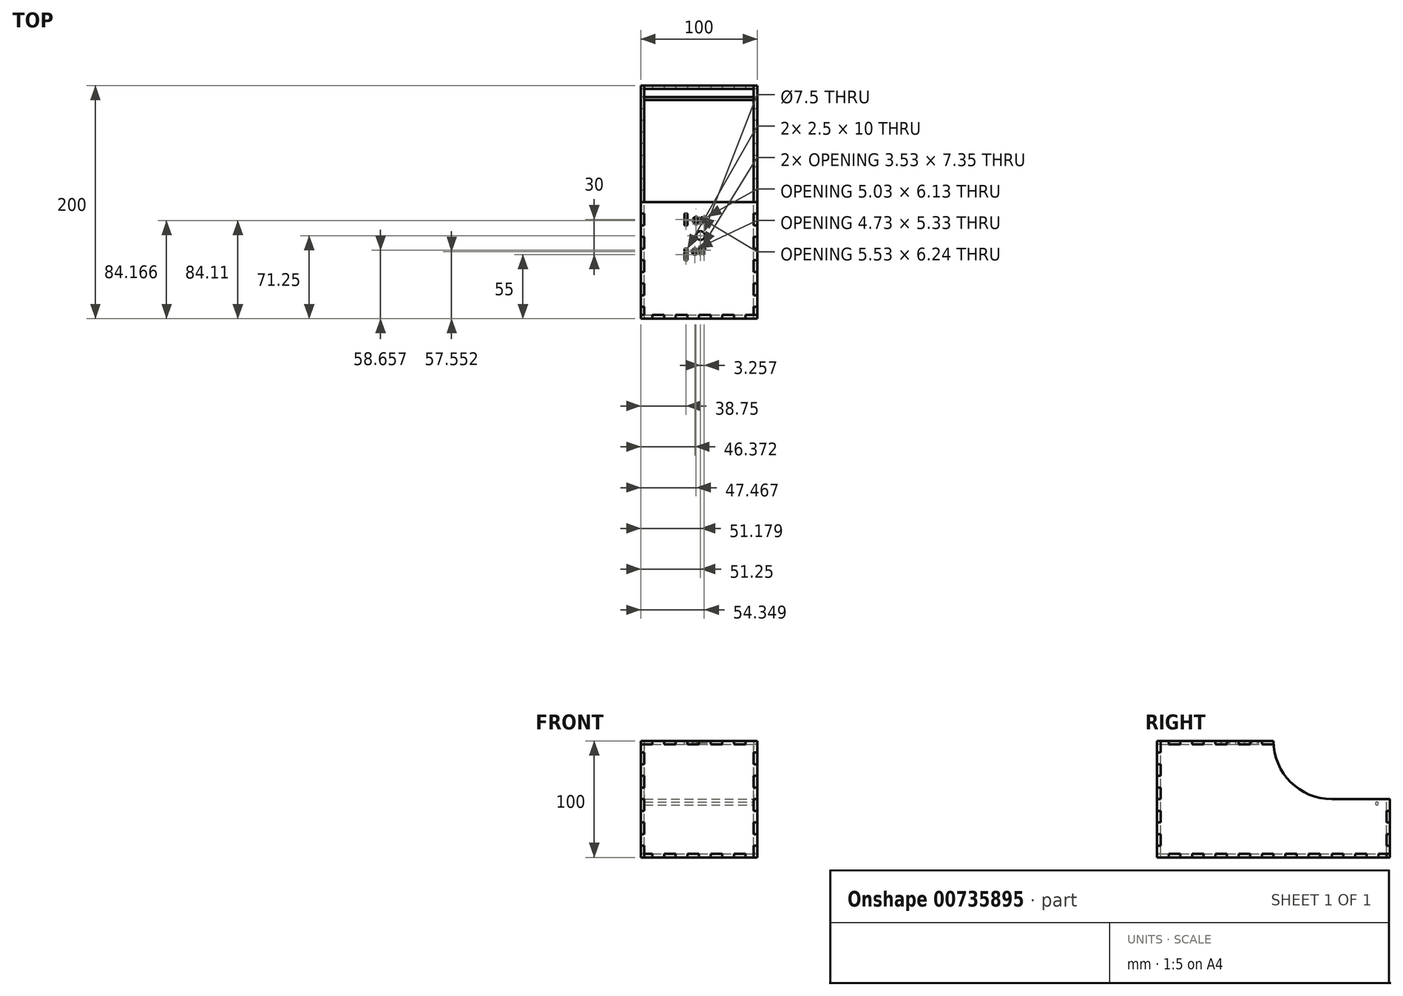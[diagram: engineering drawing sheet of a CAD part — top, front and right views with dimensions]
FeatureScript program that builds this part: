
annotation { "Feature Type Name" : "Feature", "Feature Type Description" : "" }
export const myFeature = defineFeature(function(context is Context, id is Id, definition is map)
    precondition{}
    {
        {
            var Q0;
            Q0=qCreatedBy(makeId("Right.planeOp"),FACE);
            var sketch = newSketch(context, id + "F0", { "sketchPlane" : qUnion([Q0])});
            skLineSegment(sketch, "E0.bottom", {"start": v(3, 0) * mm, "end": v(10, 0) * mm});
            skLineSegment(sketch, "E0.top", {"start": v(0, -100) * mm, "end": v(10, -100) * mm});
            skLineSegment(sketch, "E0.left", {"start": v(0, -10) * mm, "end": v(0, -20) * mm});
            skLineSegment(sketch, "E0.right", {"start": v(200, -10) * mm, "end": v(200, -20) * mm});
            skArc(sketch, "E1", {"start": v(100, 0) * mm, "mid": v(114.64, -35.36) * mm, "end": v(150, -50) * mm});
            skLineSegment(sketch, "E2", {"start": v(200, -50) * mm, "end": v(150, -50) * mm});
            skLineSegment(sketch, "E3.bottom", {"start": v(0, -90) * mm, "end": v(3, -90) * mm});
            skLineSegment(sketch, "E3.top", {"start": v(0, -80) * mm, "end": v(3, -80) * mm});
            skLineSegment(sketch, "E3.right", {"start": v(3, -90) * mm, "end": v(3, -80) * mm});
            skLineSegment(sketch, "E4.trimOffspring", {"start": v(0, -90) * mm, "end": v(0, -100) * mm});
            skLineSegment(sketch, "E5.0.1.0", {"start": v(0, -70) * mm, "end": v(3, -70) * mm});
            skLineSegment(sketch, "E5.0.1.1", {"start": v(3, -70) * mm, "end": v(3, -60) * mm});
            skLineSegment(sketch, "E5.0.1.2", {"start": v(0, -60) * mm, "end": v(3, -60) * mm});
            skLineSegment(sketch, "E5.0.2.0", {"start": v(0, -50) * mm, "end": v(3, -50) * mm});
            skLineSegment(sketch, "E5.0.2.1", {"start": v(3, -50) * mm, "end": v(3, -40) * mm});
            skLineSegment(sketch, "E5.0.2.2", {"start": v(0, -40) * mm, "end": v(3, -40) * mm});
            skLineSegment(sketch, "E5.0.3.0", {"start": v(0, -30) * mm, "end": v(3, -30) * mm});
            skLineSegment(sketch, "E5.0.3.1", {"start": v(3, -30) * mm, "end": v(3, -20) * mm});
            skLineSegment(sketch, "E5.0.3.2", {"start": v(0, -20) * mm, "end": v(3, -20) * mm});
            skLineSegment(sketch, "E5.0.4.0", {"start": v(0, -10) * mm, "end": v(3, -10) * mm});
            skLineSegment(sketch, "E5.0.4.1", {"start": v(3, -10) * mm, "end": v(3, 0) * mm});
            skLineSegment(sketch, "E5.direction1", {"start": v(0, -90) * mm, "end": v(25, -90) * mm, "construction": true});
            skLineSegment(sketch, "E5.direction2", {"start": v(0, -90) * mm, "end": v(0, -70) * mm, "construction": true});
            skLineSegment(sketch, "E6.trimOffspring", {"start": v(0, -30) * mm, "end": v(0, -40) * mm});
            skLineSegment(sketch, "E7.trimOffspring", {"start": v(0, -50) * mm, "end": v(0, -60) * mm});
            skLineSegment(sketch, "E8.trimOffspring", {"start": v(0, -70) * mm, "end": v(0, -80) * mm});
            skLineSegment(sketch, "E9.top", {"start": v(10, -97) * mm, "end": v(20, -97) * mm});
            skLineSegment(sketch, "E9.left", {"start": v(10, -100) * mm, "end": v(10, -97) * mm});
            skLineSegment(sketch, "E9.right", {"start": v(20, -100) * mm, "end": v(20, -97) * mm});
            skLineSegment(sketch, "E10.trimOffspring", {"start": v(20, -100) * mm, "end": v(30, -100) * mm});
            skLineSegment(sketch, "E11.1.0.0", {"start": v(30, -97) * mm, "end": v(40, -97) * mm});
            skLineSegment(sketch, "E11.1.0.1", {"start": v(40, -100) * mm, "end": v(40, -97) * mm});
            skLineSegment(sketch, "E11.1.0.3", {"start": v(30, -100) * mm, "end": v(30, -97) * mm});
            skLineSegment(sketch, "E11.2.0.0", {"start": v(50, -97) * mm, "end": v(60, -97) * mm});
            skLineSegment(sketch, "E11.2.0.1", {"start": v(60, -100) * mm, "end": v(60, -97) * mm});
            skLineSegment(sketch, "E11.2.0.2", {"start": v(40, -100) * mm, "end": v(50, -100) * mm});
            skLineSegment(sketch, "E11.2.0.3", {"start": v(50, -100) * mm, "end": v(50, -97) * mm});
            skLineSegment(sketch, "E11.3.0.0", {"start": v(70, -97) * mm, "end": v(80, -97) * mm});
            skLineSegment(sketch, "E11.3.0.1", {"start": v(80, -100) * mm, "end": v(80, -97) * mm});
            skLineSegment(sketch, "E11.3.0.2", {"start": v(60, -100) * mm, "end": v(70, -100) * mm});
            skLineSegment(sketch, "E11.3.0.3", {"start": v(70, -100) * mm, "end": v(70, -97) * mm});
            skLineSegment(sketch, "E11.4.0.0", {"start": v(90, -97) * mm, "end": v(100, -97) * mm});
            skLineSegment(sketch, "E11.4.0.1", {"start": v(100, -100) * mm, "end": v(100, -97) * mm});
            skLineSegment(sketch, "E11.4.0.2", {"start": v(80, -100) * mm, "end": v(90, -100) * mm});
            skLineSegment(sketch, "E11.4.0.3", {"start": v(90, -100) * mm, "end": v(90, -97) * mm});
            skLineSegment(sketch, "E11.5.0.0", {"start": v(110, -97) * mm, "end": v(120, -97) * mm});
            skLineSegment(sketch, "E11.5.0.1", {"start": v(120, -100) * mm, "end": v(120, -97) * mm});
            skLineSegment(sketch, "E11.5.0.2", {"start": v(100, -100) * mm, "end": v(110, -100) * mm});
            skLineSegment(sketch, "E11.5.0.3", {"start": v(110, -100) * mm, "end": v(110, -97) * mm});
            skLineSegment(sketch, "E11.6.0.0", {"start": v(130, -97) * mm, "end": v(140, -97) * mm});
            skLineSegment(sketch, "E11.6.0.1", {"start": v(140, -100) * mm, "end": v(140, -97) * mm});
            skLineSegment(sketch, "E11.6.0.2", {"start": v(120, -100) * mm, "end": v(130, -100) * mm});
            skLineSegment(sketch, "E11.6.0.3", {"start": v(130, -100) * mm, "end": v(130, -97) * mm});
            skLineSegment(sketch, "E11.7.0.0", {"start": v(150, -97) * mm, "end": v(160, -97) * mm});
            skLineSegment(sketch, "E11.7.0.1", {"start": v(160, -100) * mm, "end": v(160, -97) * mm});
            skLineSegment(sketch, "E11.7.0.2", {"start": v(140, -100) * mm, "end": v(150, -100) * mm});
            skLineSegment(sketch, "E11.7.0.3", {"start": v(150, -100) * mm, "end": v(150, -97) * mm});
            skLineSegment(sketch, "E11.8.0.0", {"start": v(170, -97) * mm, "end": v(180, -97) * mm});
            skLineSegment(sketch, "E11.8.0.1", {"start": v(180, -100) * mm, "end": v(180, -97) * mm});
            skLineSegment(sketch, "E11.8.0.2", {"start": v(160, -100) * mm, "end": v(170, -100) * mm});
            skLineSegment(sketch, "E11.8.0.3", {"start": v(170, -100) * mm, "end": v(170, -97) * mm});
            skLineSegment(sketch, "E11.9.0.0", {"start": v(190, -97) * mm, "end": v(200, -97) * mm});
            skLineSegment(sketch, "E11.9.0.2", {"start": v(180, -100) * mm, "end": v(190, -100) * mm});
            skLineSegment(sketch, "E11.9.0.3", {"start": v(190, -100) * mm, "end": v(190, -97) * mm});
            skLineSegment(sketch, "E11.direction1", {"start": v(0, -100) * mm, "end": v(20, -100) * mm, "construction": true});
            skLineSegment(sketch, "E12.top", {"start": v(197, -10) * mm, "end": v(200, -10) * mm});
            skLineSegment(sketch, "E12.left", {"start": v(197, -3) * mm, "end": v(197, -10) * mm});
            skLineSegment(sketch, "E13.0.1.1", {"start": v(197, -20) * mm, "end": v(197, -30) * mm});
            skLineSegment(sketch, "E13.0.1.2", {"start": v(197, -30) * mm, "end": v(200, -30) * mm});
            skLineSegment(sketch, "E13.0.1.3", {"start": v(197, -20) * mm, "end": v(200, -20) * mm});
            skLineSegment(sketch, "E13.0.2.1", {"start": v(197, -40) * mm, "end": v(197, -50) * mm});
            skLineSegment(sketch, "E13.0.2.2", {"start": v(197, -50) * mm, "end": v(200, -50) * mm});
            skLineSegment(sketch, "E13.0.2.3", {"start": v(197, -40) * mm, "end": v(200, -40) * mm});
            skLineSegment(sketch, "E13.0.3.1", {"start": v(197, -60) * mm, "end": v(197, -70) * mm});
            skLineSegment(sketch, "E13.0.3.2", {"start": v(197, -70) * mm, "end": v(200, -70) * mm});
            skLineSegment(sketch, "E13.0.3.3", {"start": v(197, -60) * mm, "end": v(200, -60) * mm});
            skLineSegment(sketch, "E13.0.4.1", {"start": v(197, -80) * mm, "end": v(197, -90) * mm});
            skLineSegment(sketch, "E13.0.4.2", {"start": v(197, -90) * mm, "end": v(200, -90) * mm});
            skLineSegment(sketch, "E13.0.4.3", {"start": v(197, -80) * mm, "end": v(200, -80) * mm});
            skLineSegment(sketch, "E13.direction1", {"start": v(197, -10) * mm, "end": v(222, -10) * mm, "construction": true});
            skLineSegment(sketch, "E13.direction2", {"start": v(197, -10) * mm, "end": v(197, -30) * mm, "construction": true});
            skLineSegment(sketch, "E14.trimOffspring", {"start": v(200, -90) * mm, "end": v(200, -97) * mm});
            skLineSegment(sketch, "E15.trimOffspring", {"start": v(200, -70) * mm, "end": v(200, -80) * mm});
            skLineSegment(sketch, "E16.trimOffspring", {"start": v(200, -50) * mm, "end": v(200, -60) * mm});
            skLineSegment(sketch, "E17.trimOffspring", {"start": v(200, -30) * mm, "end": v(200, -40) * mm});
            skLineSegment(sketch, "E18.top", {"start": v(10, -3) * mm, "end": v(20, -3) * mm});
            skLineSegment(sketch, "E18.left", {"start": v(10, 0) * mm, "end": v(10, -3) * mm});
            skLineSegment(sketch, "E18.right", {"start": v(20, 0) * mm, "end": v(20, -3) * mm});
            skLineSegment(sketch, "E19.trimOffspring", {"start": v(20, 0) * mm, "end": v(30, 0) * mm});
            skLineSegment(sketch, "E20.1.0.0", {"start": v(30, -3) * mm, "end": v(40, -3) * mm});
            skLineSegment(sketch, "E20.1.0.1", {"start": v(40, 0) * mm, "end": v(40, -3) * mm});
            skLineSegment(sketch, "E20.1.0.2", {"start": v(30, 0) * mm, "end": v(30, -3) * mm});
            skLineSegment(sketch, "E20.2.0.0", {"start": v(50, -3) * mm, "end": v(60, -3) * mm});
            skLineSegment(sketch, "E20.2.0.1", {"start": v(60, 0) * mm, "end": v(60, -3) * mm});
            skLineSegment(sketch, "E20.2.0.2", {"start": v(50, 0) * mm, "end": v(50, -3) * mm});
            skLineSegment(sketch, "E20.3.0.0", {"start": v(70, -3) * mm, "end": v(80, -3) * mm});
            skLineSegment(sketch, "E20.3.0.1", {"start": v(80, 0) * mm, "end": v(80, -3) * mm});
            skLineSegment(sketch, "E20.3.0.2", {"start": v(70, 0) * mm, "end": v(70, -3) * mm});
            skLineSegment(sketch, "E20.4.0.0", {"start": v(90, -3) * mm, "end": v(100, -3) * mm});
            skLineSegment(sketch, "E20.4.0.1", {"start": v(100, 0) * mm, "end": v(100, -3) * mm});
            skLineSegment(sketch, "E20.4.0.2", {"start": v(90, 0) * mm, "end": v(90, -3) * mm});
            skLineSegment(sketch, "E20.5.0.0", {"start": v(110, -3) * mm, "end": v(120, -3) * mm});
            skLineSegment(sketch, "E20.5.0.1", {"start": v(120, 0) * mm, "end": v(120, -3) * mm});
            skLineSegment(sketch, "E20.5.0.2", {"start": v(110, 0) * mm, "end": v(110, -3) * mm});
            skLineSegment(sketch, "E20.6.0.0", {"start": v(130, -3) * mm, "end": v(140, -3) * mm});
            skLineSegment(sketch, "E20.6.0.1", {"start": v(140, 0) * mm, "end": v(140, -3) * mm});
            skLineSegment(sketch, "E20.6.0.2", {"start": v(130, 0) * mm, "end": v(130, -3) * mm});
            skLineSegment(sketch, "E20.7.0.0", {"start": v(150, -3) * mm, "end": v(160, -3) * mm});
            skLineSegment(sketch, "E20.7.0.1", {"start": v(160, 0) * mm, "end": v(160, -3) * mm});
            skLineSegment(sketch, "E20.7.0.2", {"start": v(150, 0) * mm, "end": v(150, -3) * mm});
            skLineSegment(sketch, "E20.8.0.0", {"start": v(170, -3) * mm, "end": v(180, -3) * mm});
            skLineSegment(sketch, "E20.8.0.1", {"start": v(180, 0) * mm, "end": v(180, -3) * mm});
            skLineSegment(sketch, "E20.8.0.2", {"start": v(170, 0) * mm, "end": v(170, -3) * mm});
            skLineSegment(sketch, "E20.9.0.0", {"start": v(190, -3) * mm, "end": v(200, -3) * mm});
            skLineSegment(sketch, "E20.9.0.2", {"start": v(190, 0) * mm, "end": v(190, -3) * mm});
            skLineSegment(sketch, "E20.direction1", {"start": v(10, -3) * mm, "end": v(30, -3) * mm, "construction": true});
            skLineSegment(sketch, "E21.trimOffspring", {"start": v(40, 0) * mm, "end": v(50, 0) * mm});
            skLineSegment(sketch, "E22.trimOffspring", {"start": v(60, 0) * mm, "end": v(70, 0) * mm});
            skLineSegment(sketch, "E23.trimOffspring", {"start": v(80, 0) * mm, "end": v(90, 0) * mm});
            skLineSegment(sketch, "E24.trimOffspring", {"start": v(100, 0) * mm, "end": v(110, 0) * mm});
            skLineSegment(sketch, "E25.trimOffspring", {"start": v(120, 0) * mm, "end": v(130, 0) * mm});
            skLineSegment(sketch, "E26.trimOffspring", {"start": v(140, 0) * mm, "end": v(150, 0) * mm});
            skLineSegment(sketch, "E27.trimOffspring", {"start": v(160, 0) * mm, "end": v(170, 0) * mm});
            skLineSegment(sketch, "E28.trimOffspring", {"start": v(180, 0) * mm, "end": v(190, 0) * mm});
            skSolve(sketch);
        }
        {
            var Q0;
            Q0=makeQuery(id+"F0.imprint","IMPRINT",FACE,{"disambiguationData":[TD([[makeQuery(id+"F0.imprint","IMPRINT",EDGE,{"derivedFrom":sQuery(id+"F0.wireOp",EDGE,"E0.bottom")}),-1.0]])]});
            extrude(context, id + "F1", {"entities" : qUnion([Q0]), "depth" : 3 * mm, "offsetDistance" : 25 * mm});
        }
        {
            var Q0;
            Q0=makeQuery(id+"F0.imprint","IMPRINT",FACE,{"disambiguationData":[TD([[makeQuery(id+"F0.imprint","IMPRINT",EDGE,{"derivedFrom":sQuery(id+"F0.wireOp",EDGE,"E0.right")}),-1.0]])]});
            extrude(context, id + "F2", {"entities" : qUnion([Q0]), "depth" : 3 * mm, "offsetDistance" : 25 * mm});
        }
        {
            var Q0;
            Q0=qCreatedBy(makeId("Front.planeOp"),FACE);
            var sketch = newSketch(context, id + "F3", { "sketchPlane" : qUnion([Q0])});
            skLineSegment(sketch, "E29.bottom", {"start": v(3, 0) * mm, "end": v(-7, 0) * mm});
            skLineSegment(sketch, "E29.top", {"start": v(3, -100) * mm, "end": v(-7, -100) * mm});
            skLineSegment(sketch, "E29.left", {"start": v(3, 0) * mm, "end": v(3, -100) * mm});
            skLineSegment(sketch, "E29.right", {"start": v(-97, -3) * mm, "end": v(-97, -100) * mm});
            skLineSegment(sketch, "E30.top", {"start": v(-97, -3) * mm, "end": v(-87, -3) * mm});
            skLineSegment(sketch, "E30.right", {"start": v(-87, 0) * mm, "end": v(-87, -3) * mm});
            skLineSegment(sketch, "E31.top", {"start": v(-97, -97) * mm, "end": v(-87, -97) * mm});
            skLineSegment(sketch, "E31.left", {"start": v(-97, -100) * mm, "end": v(-97, -97) * mm});
            skLineSegment(sketch, "E31.right", {"start": v(-87, -100) * mm, "end": v(-87, -97) * mm});
            skLineSegment(sketch, "E32.1.0.0", {"start": v(-67, 0) * mm, "end": v(-67, -3) * mm});
            skLineSegment(sketch, "E32.1.0.1", {"start": v(-77, 0) * mm, "end": v(-77, -3) * mm});
            skLineSegment(sketch, "E32.1.0.2", {"start": v(-77, -3) * mm, "end": v(-67, -3) * mm});
            skLineSegment(sketch, "E32.2.0.0", {"start": v(-47, 0) * mm, "end": v(-47, -3) * mm});
            skLineSegment(sketch, "E32.2.0.1", {"start": v(-57, 0) * mm, "end": v(-57, -3) * mm});
            skLineSegment(sketch, "E32.2.0.2", {"start": v(-57, -3) * mm, "end": v(-47, -3) * mm});
            skLineSegment(sketch, "E32.3.0.0", {"start": v(-27, 0) * mm, "end": v(-27, -3) * mm});
            skLineSegment(sketch, "E32.3.0.1", {"start": v(-37, 0) * mm, "end": v(-37, -3) * mm});
            skLineSegment(sketch, "E32.3.0.2", {"start": v(-37, -3) * mm, "end": v(-27, -3) * mm});
            skLineSegment(sketch, "E32.4.0.0", {"start": v(-7, 0) * mm, "end": v(-7, -3) * mm});
            skLineSegment(sketch, "E32.4.0.1", {"start": v(-17, 0) * mm, "end": v(-17, -3) * mm});
            skLineSegment(sketch, "E32.4.0.2", {"start": v(-17, -3) * mm, "end": v(-7, -3) * mm});
            skLineSegment(sketch, "E32.direction1", {"start": v(-97, -3) * mm, "end": v(-77, -3) * mm, "construction": true});
            skLineSegment(sketch, "E33.1.0.1", {"start": v(-77, -97) * mm, "end": v(-67, -97) * mm});
            skLineSegment(sketch, "E33.1.0.2", {"start": v(-77, -100) * mm, "end": v(-77, -97) * mm});
            skLineSegment(sketch, "E33.1.0.3", {"start": v(-67, -100) * mm, "end": v(-67, -97) * mm});
            skLineSegment(sketch, "E33.2.0.1", {"start": v(-57, -97) * mm, "end": v(-47, -97) * mm});
            skLineSegment(sketch, "E33.2.0.2", {"start": v(-57, -100) * mm, "end": v(-57, -97) * mm});
            skLineSegment(sketch, "E33.2.0.3", {"start": v(-47, -100) * mm, "end": v(-47, -97) * mm});
            skLineSegment(sketch, "E33.3.0.1", {"start": v(-37, -97) * mm, "end": v(-27, -97) * mm});
            skLineSegment(sketch, "E33.3.0.2", {"start": v(-37, -100) * mm, "end": v(-37, -97) * mm});
            skLineSegment(sketch, "E33.3.0.3", {"start": v(-27, -100) * mm, "end": v(-27, -97) * mm});
            skLineSegment(sketch, "E33.4.0.1", {"start": v(-17, -97) * mm, "end": v(-7, -97) * mm});
            skLineSegment(sketch, "E33.4.0.2", {"start": v(-17, -100) * mm, "end": v(-17, -97) * mm});
            skLineSegment(sketch, "E33.4.0.3", {"start": v(-7, -100) * mm, "end": v(-7, -97) * mm});
            skLineSegment(sketch, "E33.direction1", {"start": v(-87, -100) * mm, "end": v(-77, -100) * mm, "construction": true});
            skLineSegment(sketch, "E34.trimOffspring", {"start": v(-77, 0) * mm, "end": v(-87, 0) * mm});
            skLineSegment(sketch, "E35.trimOffspring", {"start": v(-57, 0) * mm, "end": v(-67, 0) * mm});
            skLineSegment(sketch, "E36.trimOffspring", {"start": v(-37, 0) * mm, "end": v(-47, 0) * mm});
            skLineSegment(sketch, "E37.trimOffspring", {"start": v(-17, 0) * mm, "end": v(-27, 0) * mm});
            skLineSegment(sketch, "E38.trimOffspring", {"start": v(-17, -100) * mm, "end": v(-27, -100) * mm});
            skLineSegment(sketch, "E39.trimOffspring", {"start": v(-37, -100) * mm, "end": v(-47, -100) * mm});
            skLineSegment(sketch, "E40.trimOffspring", {"start": v(-57, -100) * mm, "end": v(-67, -100) * mm});
            skLineSegment(sketch, "E41.trimOffspring", {"start": v(-77, -100) * mm, "end": v(-87, -100) * mm});
            skLineSegment(sketch, "E42", {"start": v(-97, -50) * mm, "end": v(3, -50) * mm});
            skSolve(sketch);
        }
        {
            var Q0;
            Q0=makeQuery(id+"F1.opExtrude","SWEPT_BODY",BODY,{"disambiguationData":[OSD([sQuery(id+"F0.wireOp",EDGE,"E0.bottom"),sQuery(id+"F0.wireOp",EDGE,"E0.top"),sQuery(id+"F0.wireOp",EDGE,"E0.left"),sQuery(id+"F0.wireOp",EDGE,"E1"),sQuery(id+"F0.wireOp",EDGE,"E2"),sQuery(id+"F0.wireOp",EDGE,"E3.bottom"),sQuery(id+"F0.wireOp",EDGE,"E3.top"),sQuery(id+"F0.wireOp",EDGE,"E3.right"),sQuery(id+"F0.wireOp",EDGE,"E4.trimOffspring"),sQuery(id+"F0.wireOp",EDGE,"E5.0.1.0"),sQuery(id+"F0.wireOp",EDGE,"E5.0.1.1"),sQuery(id+"F0.wireOp",EDGE,"E5.0.1.2"),sQuery(id+"F0.wireOp",EDGE,"E5.0.2.0"),sQuery(id+"F0.wireOp",EDGE,"E5.0.2.1"),sQuery(id+"F0.wireOp",EDGE,"E5.0.2.2"),sQuery(id+"F0.wireOp",EDGE,"E5.0.3.0"),sQuery(id+"F0.wireOp",EDGE,"E5.0.3.1"),sQuery(id+"F0.wireOp",EDGE,"E5.0.3.2"),sQuery(id+"F0.wireOp",EDGE,"E5.0.4.0"),sQuery(id+"F0.wireOp",EDGE,"E5.0.4.1"),sQuery(id+"F0.wireOp",EDGE,"E6.trimOffspring"),sQuery(id+"F0.wireOp",EDGE,"E7.trimOffspring"),sQuery(id+"F0.wireOp",EDGE,"E8.trimOffspring"),sQuery(id+"F0.wireOp",EDGE,"E9.top"),sQuery(id+"F0.wireOp",EDGE,"E9.left"),sQuery(id+"F0.wireOp",EDGE,"E9.right"),sQuery(id+"F0.wireOp",EDGE,"E11.1.0.0"),sQuery(id+"F0.wireOp",EDGE,"E11.1.0.1"),sQuery(id+"F0.wireOp",EDGE,"E10.trimOffspring"),sQuery(id+"F0.wireOp",EDGE,"E11.1.0.3"),sQuery(id+"F0.wireOp",EDGE,"E11.2.0.0"),sQuery(id+"F0.wireOp",EDGE,"E11.2.0.1"),sQuery(id+"F0.wireOp",EDGE,"E11.2.0.3"),sQuery(id+"F0.wireOp",EDGE,"E11.3.0.0"),sQuery(id+"F0.wireOp",EDGE,"E11.3.0.1"),sQuery(id+"F0.wireOp",EDGE,"E11.3.0.3"),sQuery(id+"F0.wireOp",EDGE,"E11.4.0.0"),sQuery(id+"F0.wireOp",EDGE,"E11.4.0.1"),sQuery(id+"F0.wireOp",EDGE,"E11.4.0.3"),sQuery(id+"F0.wireOp",EDGE,"E11.5.0.0"),sQuery(id+"F0.wireOp",EDGE,"E11.5.0.1"),sQuery(id+"F0.wireOp",EDGE,"E11.5.0.3"),sQuery(id+"F0.wireOp",EDGE,"E11.6.0.0"),sQuery(id+"F0.wireOp",EDGE,"E11.6.0.1"),sQuery(id+"F0.wireOp",EDGE,"E11.6.0.3"),sQuery(id+"F0.wireOp",EDGE,"E11.7.0.0"),sQuery(id+"F0.wireOp",EDGE,"E11.7.0.1"),sQuery(id+"F0.wireOp",EDGE,"E11.7.0.3"),sQuery(id+"F0.wireOp",EDGE,"E11.8.0.0"),sQuery(id+"F0.wireOp",EDGE,"E11.8.0.1"),sQuery(id+"F0.wireOp",EDGE,"E11.8.0.3"),sQuery(id+"F0.wireOp",EDGE,"E11.9.0.0"),sQuery(id+"F0.wireOp",EDGE,"E11.9.0.3"),sQuery(id+"F0.wireOp",EDGE,"E11.2.0.2"),sQuery(id+"F0.wireOp",EDGE,"E11.3.0.2"),sQuery(id+"F0.wireOp",EDGE,"E11.4.0.2"),sQuery(id+"F0.wireOp",EDGE,"E11.5.0.2"),sQuery(id+"F0.wireOp",EDGE,"E11.6.0.2"),sQuery(id+"F0.wireOp",EDGE,"E11.7.0.2"),sQuery(id+"F0.wireOp",EDGE,"E11.8.0.2"),sQuery(id+"F0.wireOp",EDGE,"E11.9.0.2"),sQuery(id+"F0.wireOp",EDGE,"E13.0.2.2"),sQuery(id+"F0.wireOp",EDGE,"E13.0.3.1"),sQuery(id+"F0.wireOp",EDGE,"E13.0.3.2"),sQuery(id+"F0.wireOp",EDGE,"E13.0.3.3"),sQuery(id+"F0.wireOp",EDGE,"E13.0.4.1"),sQuery(id+"F0.wireOp",EDGE,"E13.0.4.2"),sQuery(id+"F0.wireOp",EDGE,"E13.0.4.3"),sQuery(id+"F0.wireOp",EDGE,"E14.trimOffspring"),sQuery(id+"F0.wireOp",EDGE,"E15.trimOffspring"),sQuery(id+"F0.wireOp",EDGE,"E16.trimOffspring"),sQuery(id+"F0.wireOp",EDGE,"E18.top"),sQuery(id+"F0.wireOp",EDGE,"E18.left"),sQuery(id+"F0.wireOp",EDGE,"E18.right"),sQuery(id+"F0.wireOp",EDGE,"E19.trimOffspring"),sQuery(id+"F0.wireOp",EDGE,"E20.1.0.0"),sQuery(id+"F0.wireOp",EDGE,"E20.1.0.1"),sQuery(id+"F0.wireOp",EDGE,"E20.1.0.2"),sQuery(id+"F0.wireOp",EDGE,"E20.2.0.0"),sQuery(id+"F0.wireOp",EDGE,"E20.2.0.1"),sQuery(id+"F0.wireOp",EDGE,"E20.2.0.2"),sQuery(id+"F0.wireOp",EDGE,"E20.3.0.0"),sQuery(id+"F0.wireOp",EDGE,"E20.3.0.1"),sQuery(id+"F0.wireOp",EDGE,"E20.3.0.2"),sQuery(id+"F0.wireOp",EDGE,"E20.4.0.0"),sQuery(id+"F0.wireOp",EDGE,"E20.4.0.1"),sQuery(id+"F0.wireOp",EDGE,"E20.4.0.2"),sQuery(id+"F0.wireOp",EDGE,"E21.trimOffspring"),sQuery(id+"F0.wireOp",EDGE,"E22.trimOffspring"),sQuery(id+"F0.wireOp",EDGE,"E23.trimOffspring")])]});
            transform(context, id + "F4", {"entities" : qUnion([Q0]), "transformType" : TransformType.TRANSLATION_3D, "dx" : -97 * mm, "dy" : 0 * mm, "dz" : 0 * mm, "makeCopy" : true});
        }
        {
            var Q0;
            Q0=makeQuery(id+"F2.opExtrude","SWEPT_BODY",BODY,{"disambiguationData":[OSD([sQuery(id+"F0.wireOp",EDGE,"E0.right"),sQuery(id+"F0.wireOp",EDGE,"E1"),sQuery(id+"F0.wireOp",EDGE,"E2"),sQuery(id+"F0.wireOp",EDGE,"E12.top"),sQuery(id+"F0.wireOp",EDGE,"E12.left"),sQuery(id+"F0.wireOp",EDGE,"E13.0.1.1"),sQuery(id+"F0.wireOp",EDGE,"E13.0.1.2"),sQuery(id+"F0.wireOp",EDGE,"E13.0.1.3"),sQuery(id+"F0.wireOp",EDGE,"E13.0.2.1"),sQuery(id+"F0.wireOp",EDGE,"E13.0.2.3"),sQuery(id+"F0.wireOp",EDGE,"E17.trimOffspring"),sQuery(id+"F0.wireOp",EDGE,"E20.5.0.0"),sQuery(id+"F0.wireOp",EDGE,"E20.5.0.1"),sQuery(id+"F0.wireOp",EDGE,"E20.5.0.2"),sQuery(id+"F0.wireOp",EDGE,"E20.6.0.0"),sQuery(id+"F0.wireOp",EDGE,"E20.6.0.1"),sQuery(id+"F0.wireOp",EDGE,"E20.6.0.2"),sQuery(id+"F0.wireOp",EDGE,"E20.7.0.0"),sQuery(id+"F0.wireOp",EDGE,"E20.7.0.1"),sQuery(id+"F0.wireOp",EDGE,"E20.7.0.2"),sQuery(id+"F0.wireOp",EDGE,"E20.8.0.0"),sQuery(id+"F0.wireOp",EDGE,"E20.8.0.1"),sQuery(id+"F0.wireOp",EDGE,"E20.8.0.2"),sQuery(id+"F0.wireOp",EDGE,"E20.9.0.0"),sQuery(id+"F0.wireOp",EDGE,"E20.9.0.2"),sQuery(id+"F0.wireOp",EDGE,"E24.trimOffspring"),sQuery(id+"F0.wireOp",EDGE,"E25.trimOffspring"),sQuery(id+"F0.wireOp",EDGE,"E26.trimOffspring"),sQuery(id+"F0.wireOp",EDGE,"E27.trimOffspring"),sQuery(id+"F0.wireOp",EDGE,"E28.trimOffspring")])]});
            transform(context, id + "F5", {"entities" : qUnion([Q0]), "transformType" : TransformType.TRANSLATION_3D, "dx" : -97 * mm, "dy" : 0 * mm, "dz" : 0 * mm, "makeCopy" : true});
        }
        {
            var Q0;
            Q0=qSketchRegion(id+"F3",true);
            extrude(context, id + "F6", {"entities" : qUnion([Q0]), "depth" : -3 * mm, "offsetDistance" : 25 * mm});
        }
        {
            var Q0;
            Q0=makeQuery(id+"F4.opPattern","COPY",BODY,{"derivedFrom":makeQuery(id+"F1.opExtrude","SWEPT_BODY",BODY,{"disambiguationData":[OSD([sQuery(id+"F0.wireOp",EDGE,"E0.bottom"),sQuery(id+"F0.wireOp",EDGE,"E0.top"),sQuery(id+"F0.wireOp",EDGE,"E0.left"),sQuery(id+"F0.wireOp",EDGE,"E1"),sQuery(id+"F0.wireOp",EDGE,"E2"),sQuery(id+"F0.wireOp",EDGE,"E3.bottom"),sQuery(id+"F0.wireOp",EDGE,"E3.top"),sQuery(id+"F0.wireOp",EDGE,"E3.right"),sQuery(id+"F0.wireOp",EDGE,"E4.trimOffspring"),sQuery(id+"F0.wireOp",EDGE,"E5.0.1.0"),sQuery(id+"F0.wireOp",EDGE,"E5.0.1.1"),sQuery(id+"F0.wireOp",EDGE,"E5.0.1.2"),sQuery(id+"F0.wireOp",EDGE,"E5.0.2.0"),sQuery(id+"F0.wireOp",EDGE,"E5.0.2.1"),sQuery(id+"F0.wireOp",EDGE,"E5.0.2.2"),sQuery(id+"F0.wireOp",EDGE,"E5.0.3.0"),sQuery(id+"F0.wireOp",EDGE,"E5.0.3.1"),sQuery(id+"F0.wireOp",EDGE,"E5.0.3.2"),sQuery(id+"F0.wireOp",EDGE,"E5.0.4.0"),sQuery(id+"F0.wireOp",EDGE,"E5.0.4.1"),sQuery(id+"F0.wireOp",EDGE,"E6.trimOffspring"),sQuery(id+"F0.wireOp",EDGE,"E7.trimOffspring"),sQuery(id+"F0.wireOp",EDGE,"E8.trimOffspring"),sQuery(id+"F0.wireOp",EDGE,"E9.top"),sQuery(id+"F0.wireOp",EDGE,"E9.left"),sQuery(id+"F0.wireOp",EDGE,"E9.right"),sQuery(id+"F0.wireOp",EDGE,"E11.1.0.0"),sQuery(id+"F0.wireOp",EDGE,"E11.1.0.1"),sQuery(id+"F0.wireOp",EDGE,"E10.trimOffspring"),sQuery(id+"F0.wireOp",EDGE,"E11.1.0.3"),sQuery(id+"F0.wireOp",EDGE,"E11.2.0.0"),sQuery(id+"F0.wireOp",EDGE,"E11.2.0.1"),sQuery(id+"F0.wireOp",EDGE,"E11.2.0.3"),sQuery(id+"F0.wireOp",EDGE,"E11.3.0.0"),sQuery(id+"F0.wireOp",EDGE,"E11.3.0.1"),sQuery(id+"F0.wireOp",EDGE,"E11.3.0.3"),sQuery(id+"F0.wireOp",EDGE,"E11.4.0.0"),sQuery(id+"F0.wireOp",EDGE,"E11.4.0.1"),sQuery(id+"F0.wireOp",EDGE,"E11.4.0.3"),sQuery(id+"F0.wireOp",EDGE,"E11.5.0.0"),sQuery(id+"F0.wireOp",EDGE,"E11.5.0.1"),sQuery(id+"F0.wireOp",EDGE,"E11.5.0.3"),sQuery(id+"F0.wireOp",EDGE,"E11.6.0.0"),sQuery(id+"F0.wireOp",EDGE,"E11.6.0.1"),sQuery(id+"F0.wireOp",EDGE,"E11.6.0.3"),sQuery(id+"F0.wireOp",EDGE,"E11.7.0.0"),sQuery(id+"F0.wireOp",EDGE,"E11.7.0.1"),sQuery(id+"F0.wireOp",EDGE,"E11.7.0.3"),sQuery(id+"F0.wireOp",EDGE,"E11.8.0.0"),sQuery(id+"F0.wireOp",EDGE,"E11.8.0.1"),sQuery(id+"F0.wireOp",EDGE,"E11.8.0.3"),sQuery(id+"F0.wireOp",EDGE,"E11.9.0.0"),sQuery(id+"F0.wireOp",EDGE,"E11.9.0.3"),sQuery(id+"F0.wireOp",EDGE,"E11.2.0.2"),sQuery(id+"F0.wireOp",EDGE,"E11.3.0.2"),sQuery(id+"F0.wireOp",EDGE,"E11.4.0.2"),sQuery(id+"F0.wireOp",EDGE,"E11.5.0.2"),sQuery(id+"F0.wireOp",EDGE,"E11.6.0.2"),sQuery(id+"F0.wireOp",EDGE,"E11.7.0.2"),sQuery(id+"F0.wireOp",EDGE,"E11.8.0.2"),sQuery(id+"F0.wireOp",EDGE,"E11.9.0.2"),sQuery(id+"F0.wireOp",EDGE,"E13.0.2.2"),sQuery(id+"F0.wireOp",EDGE,"E13.0.3.1"),sQuery(id+"F0.wireOp",EDGE,"E13.0.3.2"),sQuery(id+"F0.wireOp",EDGE,"E13.0.3.3"),sQuery(id+"F0.wireOp",EDGE,"E13.0.4.1"),sQuery(id+"F0.wireOp",EDGE,"E13.0.4.2"),sQuery(id+"F0.wireOp",EDGE,"E13.0.4.3"),sQuery(id+"F0.wireOp",EDGE,"E14.trimOffspring"),sQuery(id+"F0.wireOp",EDGE,"E15.trimOffspring"),sQuery(id+"F0.wireOp",EDGE,"E16.trimOffspring"),sQuery(id+"F0.wireOp",EDGE,"E18.top"),sQuery(id+"F0.wireOp",EDGE,"E18.left"),sQuery(id+"F0.wireOp",EDGE,"E18.right"),sQuery(id+"F0.wireOp",EDGE,"E19.trimOffspring"),sQuery(id+"F0.wireOp",EDGE,"E20.1.0.0"),sQuery(id+"F0.wireOp",EDGE,"E20.1.0.1"),sQuery(id+"F0.wireOp",EDGE,"E20.1.0.2"),sQuery(id+"F0.wireOp",EDGE,"E20.2.0.0"),sQuery(id+"F0.wireOp",EDGE,"E20.2.0.1"),sQuery(id+"F0.wireOp",EDGE,"E20.2.0.2"),sQuery(id+"F0.wireOp",EDGE,"E20.3.0.0"),sQuery(id+"F0.wireOp",EDGE,"E20.3.0.1"),sQuery(id+"F0.wireOp",EDGE,"E20.3.0.2"),sQuery(id+"F0.wireOp",EDGE,"E20.4.0.0"),sQuery(id+"F0.wireOp",EDGE,"E20.4.0.1"),sQuery(id+"F0.wireOp",EDGE,"E20.4.0.2"),sQuery(id+"F0.wireOp",EDGE,"E21.trimOffspring"),sQuery(id+"F0.wireOp",EDGE,"E22.trimOffspring"),sQuery(id+"F0.wireOp",EDGE,"E23.trimOffspring")])]}),"instanceName":"1"});
            var Q1;
            Q1=makeQuery(id+"F1.opExtrude","SWEPT_BODY",BODY,{"disambiguationData":[OSD([sQuery(id+"F0.wireOp",EDGE,"E0.bottom"),sQuery(id+"F0.wireOp",EDGE,"E0.top"),sQuery(id+"F0.wireOp",EDGE,"E0.left"),sQuery(id+"F0.wireOp",EDGE,"E1"),sQuery(id+"F0.wireOp",EDGE,"E2"),sQuery(id+"F0.wireOp",EDGE,"E3.bottom"),sQuery(id+"F0.wireOp",EDGE,"E3.top"),sQuery(id+"F0.wireOp",EDGE,"E3.right"),sQuery(id+"F0.wireOp",EDGE,"E4.trimOffspring"),sQuery(id+"F0.wireOp",EDGE,"E5.0.1.0"),sQuery(id+"F0.wireOp",EDGE,"E5.0.1.1"),sQuery(id+"F0.wireOp",EDGE,"E5.0.1.2"),sQuery(id+"F0.wireOp",EDGE,"E5.0.2.0"),sQuery(id+"F0.wireOp",EDGE,"E5.0.2.1"),sQuery(id+"F0.wireOp",EDGE,"E5.0.2.2"),sQuery(id+"F0.wireOp",EDGE,"E5.0.3.0"),sQuery(id+"F0.wireOp",EDGE,"E5.0.3.1"),sQuery(id+"F0.wireOp",EDGE,"E5.0.3.2"),sQuery(id+"F0.wireOp",EDGE,"E5.0.4.0"),sQuery(id+"F0.wireOp",EDGE,"E5.0.4.1"),sQuery(id+"F0.wireOp",EDGE,"E6.trimOffspring"),sQuery(id+"F0.wireOp",EDGE,"E7.trimOffspring"),sQuery(id+"F0.wireOp",EDGE,"E8.trimOffspring"),sQuery(id+"F0.wireOp",EDGE,"E9.top"),sQuery(id+"F0.wireOp",EDGE,"E9.left"),sQuery(id+"F0.wireOp",EDGE,"E9.right"),sQuery(id+"F0.wireOp",EDGE,"E11.1.0.0"),sQuery(id+"F0.wireOp",EDGE,"E11.1.0.1"),sQuery(id+"F0.wireOp",EDGE,"E10.trimOffspring"),sQuery(id+"F0.wireOp",EDGE,"E11.1.0.3"),sQuery(id+"F0.wireOp",EDGE,"E11.2.0.0"),sQuery(id+"F0.wireOp",EDGE,"E11.2.0.1"),sQuery(id+"F0.wireOp",EDGE,"E11.2.0.3"),sQuery(id+"F0.wireOp",EDGE,"E11.3.0.0"),sQuery(id+"F0.wireOp",EDGE,"E11.3.0.1"),sQuery(id+"F0.wireOp",EDGE,"E11.3.0.3"),sQuery(id+"F0.wireOp",EDGE,"E11.4.0.0"),sQuery(id+"F0.wireOp",EDGE,"E11.4.0.1"),sQuery(id+"F0.wireOp",EDGE,"E11.4.0.3"),sQuery(id+"F0.wireOp",EDGE,"E11.5.0.0"),sQuery(id+"F0.wireOp",EDGE,"E11.5.0.1"),sQuery(id+"F0.wireOp",EDGE,"E11.5.0.3"),sQuery(id+"F0.wireOp",EDGE,"E11.6.0.0"),sQuery(id+"F0.wireOp",EDGE,"E11.6.0.1"),sQuery(id+"F0.wireOp",EDGE,"E11.6.0.3"),sQuery(id+"F0.wireOp",EDGE,"E11.7.0.0"),sQuery(id+"F0.wireOp",EDGE,"E11.7.0.1"),sQuery(id+"F0.wireOp",EDGE,"E11.7.0.3"),sQuery(id+"F0.wireOp",EDGE,"E11.8.0.0"),sQuery(id+"F0.wireOp",EDGE,"E11.8.0.1"),sQuery(id+"F0.wireOp",EDGE,"E11.8.0.3"),sQuery(id+"F0.wireOp",EDGE,"E11.9.0.0"),sQuery(id+"F0.wireOp",EDGE,"E11.9.0.3"),sQuery(id+"F0.wireOp",EDGE,"E11.2.0.2"),sQuery(id+"F0.wireOp",EDGE,"E11.3.0.2"),sQuery(id+"F0.wireOp",EDGE,"E11.4.0.2"),sQuery(id+"F0.wireOp",EDGE,"E11.5.0.2"),sQuery(id+"F0.wireOp",EDGE,"E11.6.0.2"),sQuery(id+"F0.wireOp",EDGE,"E11.7.0.2"),sQuery(id+"F0.wireOp",EDGE,"E11.8.0.2"),sQuery(id+"F0.wireOp",EDGE,"E11.9.0.2"),sQuery(id+"F0.wireOp",EDGE,"E13.0.2.2"),sQuery(id+"F0.wireOp",EDGE,"E13.0.3.1"),sQuery(id+"F0.wireOp",EDGE,"E13.0.3.2"),sQuery(id+"F0.wireOp",EDGE,"E13.0.3.3"),sQuery(id+"F0.wireOp",EDGE,"E13.0.4.1"),sQuery(id+"F0.wireOp",EDGE,"E13.0.4.2"),sQuery(id+"F0.wireOp",EDGE,"E13.0.4.3"),sQuery(id+"F0.wireOp",EDGE,"E14.trimOffspring"),sQuery(id+"F0.wireOp",EDGE,"E15.trimOffspring"),sQuery(id+"F0.wireOp",EDGE,"E16.trimOffspring"),sQuery(id+"F0.wireOp",EDGE,"E18.top"),sQuery(id+"F0.wireOp",EDGE,"E18.left"),sQuery(id+"F0.wireOp",EDGE,"E18.right"),sQuery(id+"F0.wireOp",EDGE,"E19.trimOffspring"),sQuery(id+"F0.wireOp",EDGE,"E20.1.0.0"),sQuery(id+"F0.wireOp",EDGE,"E20.1.0.1"),sQuery(id+"F0.wireOp",EDGE,"E20.1.0.2"),sQuery(id+"F0.wireOp",EDGE,"E20.2.0.0"),sQuery(id+"F0.wireOp",EDGE,"E20.2.0.1"),sQuery(id+"F0.wireOp",EDGE,"E20.2.0.2"),sQuery(id+"F0.wireOp",EDGE,"E20.3.0.0"),sQuery(id+"F0.wireOp",EDGE,"E20.3.0.1"),sQuery(id+"F0.wireOp",EDGE,"E20.3.0.2"),sQuery(id+"F0.wireOp",EDGE,"E20.4.0.0"),sQuery(id+"F0.wireOp",EDGE,"E20.4.0.1"),sQuery(id+"F0.wireOp",EDGE,"E20.4.0.2"),sQuery(id+"F0.wireOp",EDGE,"E21.trimOffspring"),sQuery(id+"F0.wireOp",EDGE,"E22.trimOffspring"),sQuery(id+"F0.wireOp",EDGE,"E23.trimOffspring")])]});
            var Q2;
            Q2=makeQuery(id+"F6.opExtrude","SWEPT_BODY",BODY,{"disambiguationData":[OSD([sQuery(id+"F3.wireOp",EDGE,"E29.bottom"),sQuery(id+"F3.wireOp",EDGE,"E29.top"),sQuery(id+"F3.wireOp",EDGE,"E29.left"),sQuery(id+"F3.wireOp",EDGE,"E29.right"),sQuery(id+"F3.wireOp",EDGE,"E30.top"),sQuery(id+"F3.wireOp",EDGE,"E30.right"),sQuery(id+"F3.wireOp",EDGE,"E31.top"),sQuery(id+"F3.wireOp",EDGE,"E31.right"),sQuery(id+"F3.wireOp",EDGE,"E32.1.0.0"),sQuery(id+"F3.wireOp",EDGE,"E32.1.0.1"),sQuery(id+"F3.wireOp",EDGE,"E32.1.0.2"),sQuery(id+"F3.wireOp",EDGE,"E32.2.0.0"),sQuery(id+"F3.wireOp",EDGE,"E32.2.0.1"),sQuery(id+"F3.wireOp",EDGE,"E32.2.0.2"),sQuery(id+"F3.wireOp",EDGE,"E32.3.0.0"),sQuery(id+"F3.wireOp",EDGE,"E32.3.0.1"),sQuery(id+"F3.wireOp",EDGE,"E32.3.0.2"),sQuery(id+"F3.wireOp",EDGE,"E32.4.0.0"),sQuery(id+"F3.wireOp",EDGE,"E32.4.0.1"),sQuery(id+"F3.wireOp",EDGE,"E32.4.0.2"),sQuery(id+"F3.wireOp",EDGE,"E33.1.0.1"),sQuery(id+"F3.wireOp",EDGE,"E33.1.0.2"),sQuery(id+"F3.wireOp",EDGE,"E33.1.0.3"),sQuery(id+"F3.wireOp",EDGE,"E33.2.0.1"),sQuery(id+"F3.wireOp",EDGE,"E33.2.0.2"),sQuery(id+"F3.wireOp",EDGE,"E33.2.0.3"),sQuery(id+"F3.wireOp",EDGE,"E33.3.0.1"),sQuery(id+"F3.wireOp",EDGE,"E33.3.0.2"),sQuery(id+"F3.wireOp",EDGE,"E33.3.0.3"),sQuery(id+"F3.wireOp",EDGE,"E33.4.0.1"),sQuery(id+"F3.wireOp",EDGE,"E33.4.0.2"),sQuery(id+"F3.wireOp",EDGE,"E33.4.0.3"),sQuery(id+"F3.wireOp",EDGE,"E34.trimOffspring"),sQuery(id+"F3.wireOp",EDGE,"E35.trimOffspring"),sQuery(id+"F3.wireOp",EDGE,"E36.trimOffspring"),sQuery(id+"F3.wireOp",EDGE,"E37.trimOffspring"),sQuery(id+"F3.wireOp",EDGE,"E38.trimOffspring"),sQuery(id+"F3.wireOp",EDGE,"E39.trimOffspring"),sQuery(id+"F3.wireOp",EDGE,"E40.trimOffspring"),sQuery(id+"F3.wireOp",EDGE,"E41.trimOffspring")])]});
            booleanBodies(context, id + "F7", {"operationType" : BooleanOperationType.SUBTRACTION, "tools" : qUnion([Q0, Q1]), "targets" : qUnion([Q2]), "keepTools" : true});
        }
        {
            var Q0;
            {var subQ1=sQuery(id+"F3.wireOp",EDGE,"E29.top");Q0=makeQuery(id+"F3.imprint","IMPRINT",FACE,{"disambiguationData":[TD([[makeQuery(id+"F3.imprint","IMPRINT",EDGE,{"derivedFrom":subQ1}),-1.0]])]});}
            extrude(context, id + "F8", {"entities" : qUnion([Q0]), "oppositeDirection" : true, "depth" : 200 * mm, "offsetDistance" : 25 * mm, "hasSecondDirection" : true, "secondDirectionOppositeDirection" : true, "secondDirectionDepth" : 197 * mm});
        }
        {
            var Q0;
            {var subQ0=sQuery(id+"F3.wireOp",EDGE,"E29.bottom");Q0=makeQuery(id+"F3.imprint","IMPRINT",FACE,{"disambiguationData":[TD([[makeQuery(id+"F3.imprint","IMPRINT",EDGE,{"derivedFrom":subQ0}),1.0]])]});}
            extrude(context, id + "F9", {"entities" : qUnion([Q0]), "oppositeDirection" : true, "depth" : 200 * mm, "offsetDistance" : 25 * mm, "hasSecondDirection" : true, "secondDirectionOppositeDirection" : true, "secondDirectionDepth" : 197 * mm});
        }
        {
            var Q0;
            Q0=makeQuery(id+"F2.opExtrude","SWEPT_BODY",BODY,{"disambiguationData":[OSD([sQuery(id+"F0.wireOp",EDGE,"E0.right"),sQuery(id+"F0.wireOp",EDGE,"E1"),sQuery(id+"F0.wireOp",EDGE,"E2"),sQuery(id+"F0.wireOp",EDGE,"E12.top"),sQuery(id+"F0.wireOp",EDGE,"E12.left"),sQuery(id+"F0.wireOp",EDGE,"E13.0.1.1"),sQuery(id+"F0.wireOp",EDGE,"E13.0.1.2"),sQuery(id+"F0.wireOp",EDGE,"E13.0.1.3"),sQuery(id+"F0.wireOp",EDGE,"E13.0.2.1"),sQuery(id+"F0.wireOp",EDGE,"E13.0.2.3"),sQuery(id+"F0.wireOp",EDGE,"E17.trimOffspring"),sQuery(id+"F0.wireOp",EDGE,"E20.5.0.0"),sQuery(id+"F0.wireOp",EDGE,"E20.5.0.1"),sQuery(id+"F0.wireOp",EDGE,"E20.5.0.2"),sQuery(id+"F0.wireOp",EDGE,"E20.6.0.0"),sQuery(id+"F0.wireOp",EDGE,"E20.6.0.1"),sQuery(id+"F0.wireOp",EDGE,"E20.6.0.2"),sQuery(id+"F0.wireOp",EDGE,"E20.7.0.0"),sQuery(id+"F0.wireOp",EDGE,"E20.7.0.1"),sQuery(id+"F0.wireOp",EDGE,"E20.7.0.2"),sQuery(id+"F0.wireOp",EDGE,"E20.8.0.0"),sQuery(id+"F0.wireOp",EDGE,"E20.8.0.1"),sQuery(id+"F0.wireOp",EDGE,"E20.8.0.2"),sQuery(id+"F0.wireOp",EDGE,"E20.9.0.0"),sQuery(id+"F0.wireOp",EDGE,"E20.9.0.2"),sQuery(id+"F0.wireOp",EDGE,"E24.trimOffspring"),sQuery(id+"F0.wireOp",EDGE,"E25.trimOffspring"),sQuery(id+"F0.wireOp",EDGE,"E26.trimOffspring"),sQuery(id+"F0.wireOp",EDGE,"E27.trimOffspring"),sQuery(id+"F0.wireOp",EDGE,"E28.trimOffspring")])]});
            var Q1;
            Q1=makeQuery(id+"F5.opPattern","COPY",BODY,{"derivedFrom":makeQuery(id+"F2.opExtrude","SWEPT_BODY",BODY,{"disambiguationData":[OSD([sQuery(id+"F0.wireOp",EDGE,"E0.right"),sQuery(id+"F0.wireOp",EDGE,"E1"),sQuery(id+"F0.wireOp",EDGE,"E2"),sQuery(id+"F0.wireOp",EDGE,"E12.top"),sQuery(id+"F0.wireOp",EDGE,"E12.left"),sQuery(id+"F0.wireOp",EDGE,"E13.0.1.1"),sQuery(id+"F0.wireOp",EDGE,"E13.0.1.2"),sQuery(id+"F0.wireOp",EDGE,"E13.0.1.3"),sQuery(id+"F0.wireOp",EDGE,"E13.0.2.1"),sQuery(id+"F0.wireOp",EDGE,"E13.0.2.3"),sQuery(id+"F0.wireOp",EDGE,"E17.trimOffspring"),sQuery(id+"F0.wireOp",EDGE,"E20.5.0.0"),sQuery(id+"F0.wireOp",EDGE,"E20.5.0.1"),sQuery(id+"F0.wireOp",EDGE,"E20.5.0.2"),sQuery(id+"F0.wireOp",EDGE,"E20.6.0.0"),sQuery(id+"F0.wireOp",EDGE,"E20.6.0.1"),sQuery(id+"F0.wireOp",EDGE,"E20.6.0.2"),sQuery(id+"F0.wireOp",EDGE,"E20.7.0.0"),sQuery(id+"F0.wireOp",EDGE,"E20.7.0.1"),sQuery(id+"F0.wireOp",EDGE,"E20.7.0.2"),sQuery(id+"F0.wireOp",EDGE,"E20.8.0.0"),sQuery(id+"F0.wireOp",EDGE,"E20.8.0.1"),sQuery(id+"F0.wireOp",EDGE,"E20.8.0.2"),sQuery(id+"F0.wireOp",EDGE,"E20.9.0.0"),sQuery(id+"F0.wireOp",EDGE,"E20.9.0.2"),sQuery(id+"F0.wireOp",EDGE,"E24.trimOffspring"),sQuery(id+"F0.wireOp",EDGE,"E25.trimOffspring"),sQuery(id+"F0.wireOp",EDGE,"E26.trimOffspring"),sQuery(id+"F0.wireOp",EDGE,"E27.trimOffspring"),sQuery(id+"F0.wireOp",EDGE,"E28.trimOffspring")])]}),"instanceName":"1"});
            var Q2;
            Q2=makeQuery(id+"F9.opExtrude","SWEPT_BODY",BODY,{"disambiguationData":[OSD([sQuery(id+"F3.wireOp",EDGE,"E29.bottom"),sQuery(id+"F3.wireOp",EDGE,"E29.left"),sQuery(id+"F3.wireOp",EDGE,"E29.right"),sQuery(id+"F3.wireOp",EDGE,"E30.top"),sQuery(id+"F3.wireOp",EDGE,"E30.right"),sQuery(id+"F3.wireOp",EDGE,"E32.1.0.0"),sQuery(id+"F3.wireOp",EDGE,"E32.1.0.1"),sQuery(id+"F3.wireOp",EDGE,"E32.1.0.2"),sQuery(id+"F3.wireOp",EDGE,"E32.2.0.0"),sQuery(id+"F3.wireOp",EDGE,"E32.2.0.1"),sQuery(id+"F3.wireOp",EDGE,"E32.2.0.2"),sQuery(id+"F3.wireOp",EDGE,"E32.3.0.0"),sQuery(id+"F3.wireOp",EDGE,"E32.3.0.1"),sQuery(id+"F3.wireOp",EDGE,"E32.3.0.2"),sQuery(id+"F3.wireOp",EDGE,"E32.4.0.0"),sQuery(id+"F3.wireOp",EDGE,"E32.4.0.1"),sQuery(id+"F3.wireOp",EDGE,"E32.4.0.2"),sQuery(id+"F3.wireOp",EDGE,"E34.trimOffspring"),sQuery(id+"F3.wireOp",EDGE,"E35.trimOffspring"),sQuery(id+"F3.wireOp",EDGE,"E36.trimOffspring"),sQuery(id+"F3.wireOp",EDGE,"E37.trimOffspring"),sQuery(id+"F3.wireOp",EDGE,"E42")])]});
            booleanBodies(context, id + "F10", {"operationType" : BooleanOperationType.SUBTRACTION, "tools" : qUnion([Q0, Q1]), "targets" : qUnion([Q2]), "keepTools" : true});
        }
        {
            var Q0;
            Q0=makeQuery(id+"F1.opExtrude","SWEPT_BODY",BODY,{"disambiguationData":[OSD([sQuery(id+"F0.wireOp",EDGE,"E0.bottom"),sQuery(id+"F0.wireOp",EDGE,"E0.top"),sQuery(id+"F0.wireOp",EDGE,"E0.left"),sQuery(id+"F0.wireOp",EDGE,"E1"),sQuery(id+"F0.wireOp",EDGE,"E2"),sQuery(id+"F0.wireOp",EDGE,"E3.bottom"),sQuery(id+"F0.wireOp",EDGE,"E3.top"),sQuery(id+"F0.wireOp",EDGE,"E3.right"),sQuery(id+"F0.wireOp",EDGE,"E4.trimOffspring"),sQuery(id+"F0.wireOp",EDGE,"E5.0.1.0"),sQuery(id+"F0.wireOp",EDGE,"E5.0.1.1"),sQuery(id+"F0.wireOp",EDGE,"E5.0.1.2"),sQuery(id+"F0.wireOp",EDGE,"E5.0.2.0"),sQuery(id+"F0.wireOp",EDGE,"E5.0.2.1"),sQuery(id+"F0.wireOp",EDGE,"E5.0.2.2"),sQuery(id+"F0.wireOp",EDGE,"E5.0.3.0"),sQuery(id+"F0.wireOp",EDGE,"E5.0.3.1"),sQuery(id+"F0.wireOp",EDGE,"E5.0.3.2"),sQuery(id+"F0.wireOp",EDGE,"E5.0.4.0"),sQuery(id+"F0.wireOp",EDGE,"E5.0.4.1"),sQuery(id+"F0.wireOp",EDGE,"E6.trimOffspring"),sQuery(id+"F0.wireOp",EDGE,"E7.trimOffspring"),sQuery(id+"F0.wireOp",EDGE,"E8.trimOffspring"),sQuery(id+"F0.wireOp",EDGE,"E9.top"),sQuery(id+"F0.wireOp",EDGE,"E9.left"),sQuery(id+"F0.wireOp",EDGE,"E9.right"),sQuery(id+"F0.wireOp",EDGE,"E11.1.0.0"),sQuery(id+"F0.wireOp",EDGE,"E11.1.0.1"),sQuery(id+"F0.wireOp",EDGE,"E10.trimOffspring"),sQuery(id+"F0.wireOp",EDGE,"E11.1.0.3"),sQuery(id+"F0.wireOp",EDGE,"E11.2.0.0"),sQuery(id+"F0.wireOp",EDGE,"E11.2.0.1"),sQuery(id+"F0.wireOp",EDGE,"E11.2.0.3"),sQuery(id+"F0.wireOp",EDGE,"E11.3.0.0"),sQuery(id+"F0.wireOp",EDGE,"E11.3.0.1"),sQuery(id+"F0.wireOp",EDGE,"E11.3.0.3"),sQuery(id+"F0.wireOp",EDGE,"E11.4.0.0"),sQuery(id+"F0.wireOp",EDGE,"E11.4.0.1"),sQuery(id+"F0.wireOp",EDGE,"E11.4.0.3"),sQuery(id+"F0.wireOp",EDGE,"E11.5.0.0"),sQuery(id+"F0.wireOp",EDGE,"E11.5.0.1"),sQuery(id+"F0.wireOp",EDGE,"E11.5.0.3"),sQuery(id+"F0.wireOp",EDGE,"E11.6.0.0"),sQuery(id+"F0.wireOp",EDGE,"E11.6.0.1"),sQuery(id+"F0.wireOp",EDGE,"E11.6.0.3"),sQuery(id+"F0.wireOp",EDGE,"E11.7.0.0"),sQuery(id+"F0.wireOp",EDGE,"E11.7.0.1"),sQuery(id+"F0.wireOp",EDGE,"E11.7.0.3"),sQuery(id+"F0.wireOp",EDGE,"E11.8.0.0"),sQuery(id+"F0.wireOp",EDGE,"E11.8.0.1"),sQuery(id+"F0.wireOp",EDGE,"E11.8.0.3"),sQuery(id+"F0.wireOp",EDGE,"E11.9.0.0"),sQuery(id+"F0.wireOp",EDGE,"E11.9.0.3"),sQuery(id+"F0.wireOp",EDGE,"E11.2.0.2"),sQuery(id+"F0.wireOp",EDGE,"E11.3.0.2"),sQuery(id+"F0.wireOp",EDGE,"E11.4.0.2"),sQuery(id+"F0.wireOp",EDGE,"E11.5.0.2"),sQuery(id+"F0.wireOp",EDGE,"E11.6.0.2"),sQuery(id+"F0.wireOp",EDGE,"E11.7.0.2"),sQuery(id+"F0.wireOp",EDGE,"E11.8.0.2"),sQuery(id+"F0.wireOp",EDGE,"E11.9.0.2"),sQuery(id+"F0.wireOp",EDGE,"E13.0.2.2"),sQuery(id+"F0.wireOp",EDGE,"E13.0.3.1"),sQuery(id+"F0.wireOp",EDGE,"E13.0.3.2"),sQuery(id+"F0.wireOp",EDGE,"E13.0.3.3"),sQuery(id+"F0.wireOp",EDGE,"E13.0.4.1"),sQuery(id+"F0.wireOp",EDGE,"E13.0.4.2"),sQuery(id+"F0.wireOp",EDGE,"E13.0.4.3"),sQuery(id+"F0.wireOp",EDGE,"E14.trimOffspring"),sQuery(id+"F0.wireOp",EDGE,"E15.trimOffspring"),sQuery(id+"F0.wireOp",EDGE,"E16.trimOffspring"),sQuery(id+"F0.wireOp",EDGE,"E18.top"),sQuery(id+"F0.wireOp",EDGE,"E18.left"),sQuery(id+"F0.wireOp",EDGE,"E18.right"),sQuery(id+"F0.wireOp",EDGE,"E19.trimOffspring"),sQuery(id+"F0.wireOp",EDGE,"E20.1.0.0"),sQuery(id+"F0.wireOp",EDGE,"E20.1.0.1"),sQuery(id+"F0.wireOp",EDGE,"E20.1.0.2"),sQuery(id+"F0.wireOp",EDGE,"E20.2.0.0"),sQuery(id+"F0.wireOp",EDGE,"E20.2.0.1"),sQuery(id+"F0.wireOp",EDGE,"E20.2.0.2"),sQuery(id+"F0.wireOp",EDGE,"E20.3.0.0"),sQuery(id+"F0.wireOp",EDGE,"E20.3.0.1"),sQuery(id+"F0.wireOp",EDGE,"E20.3.0.2"),sQuery(id+"F0.wireOp",EDGE,"E20.4.0.0"),sQuery(id+"F0.wireOp",EDGE,"E20.4.0.1"),sQuery(id+"F0.wireOp",EDGE,"E20.4.0.2"),sQuery(id+"F0.wireOp",EDGE,"E21.trimOffspring"),sQuery(id+"F0.wireOp",EDGE,"E22.trimOffspring"),sQuery(id+"F0.wireOp",EDGE,"E23.trimOffspring")])]});
            var Q1;
            Q1=makeQuery(id+"F4.opPattern","COPY",BODY,{"derivedFrom":makeQuery(id+"F1.opExtrude","SWEPT_BODY",BODY,{"disambiguationData":[OSD([sQuery(id+"F0.wireOp",EDGE,"E0.bottom"),sQuery(id+"F0.wireOp",EDGE,"E0.top"),sQuery(id+"F0.wireOp",EDGE,"E0.left"),sQuery(id+"F0.wireOp",EDGE,"E1"),sQuery(id+"F0.wireOp",EDGE,"E2"),sQuery(id+"F0.wireOp",EDGE,"E3.bottom"),sQuery(id+"F0.wireOp",EDGE,"E3.top"),sQuery(id+"F0.wireOp",EDGE,"E3.right"),sQuery(id+"F0.wireOp",EDGE,"E4.trimOffspring"),sQuery(id+"F0.wireOp",EDGE,"E5.0.1.0"),sQuery(id+"F0.wireOp",EDGE,"E5.0.1.1"),sQuery(id+"F0.wireOp",EDGE,"E5.0.1.2"),sQuery(id+"F0.wireOp",EDGE,"E5.0.2.0"),sQuery(id+"F0.wireOp",EDGE,"E5.0.2.1"),sQuery(id+"F0.wireOp",EDGE,"E5.0.2.2"),sQuery(id+"F0.wireOp",EDGE,"E5.0.3.0"),sQuery(id+"F0.wireOp",EDGE,"E5.0.3.1"),sQuery(id+"F0.wireOp",EDGE,"E5.0.3.2"),sQuery(id+"F0.wireOp",EDGE,"E5.0.4.0"),sQuery(id+"F0.wireOp",EDGE,"E5.0.4.1"),sQuery(id+"F0.wireOp",EDGE,"E6.trimOffspring"),sQuery(id+"F0.wireOp",EDGE,"E7.trimOffspring"),sQuery(id+"F0.wireOp",EDGE,"E8.trimOffspring"),sQuery(id+"F0.wireOp",EDGE,"E9.top"),sQuery(id+"F0.wireOp",EDGE,"E9.left"),sQuery(id+"F0.wireOp",EDGE,"E9.right"),sQuery(id+"F0.wireOp",EDGE,"E11.1.0.0"),sQuery(id+"F0.wireOp",EDGE,"E11.1.0.1"),sQuery(id+"F0.wireOp",EDGE,"E10.trimOffspring"),sQuery(id+"F0.wireOp",EDGE,"E11.1.0.3"),sQuery(id+"F0.wireOp",EDGE,"E11.2.0.0"),sQuery(id+"F0.wireOp",EDGE,"E11.2.0.1"),sQuery(id+"F0.wireOp",EDGE,"E11.2.0.3"),sQuery(id+"F0.wireOp",EDGE,"E11.3.0.0"),sQuery(id+"F0.wireOp",EDGE,"E11.3.0.1"),sQuery(id+"F0.wireOp",EDGE,"E11.3.0.3"),sQuery(id+"F0.wireOp",EDGE,"E11.4.0.0"),sQuery(id+"F0.wireOp",EDGE,"E11.4.0.1"),sQuery(id+"F0.wireOp",EDGE,"E11.4.0.3"),sQuery(id+"F0.wireOp",EDGE,"E11.5.0.0"),sQuery(id+"F0.wireOp",EDGE,"E11.5.0.1"),sQuery(id+"F0.wireOp",EDGE,"E11.5.0.3"),sQuery(id+"F0.wireOp",EDGE,"E11.6.0.0"),sQuery(id+"F0.wireOp",EDGE,"E11.6.0.1"),sQuery(id+"F0.wireOp",EDGE,"E11.6.0.3"),sQuery(id+"F0.wireOp",EDGE,"E11.7.0.0"),sQuery(id+"F0.wireOp",EDGE,"E11.7.0.1"),sQuery(id+"F0.wireOp",EDGE,"E11.7.0.3"),sQuery(id+"F0.wireOp",EDGE,"E11.8.0.0"),sQuery(id+"F0.wireOp",EDGE,"E11.8.0.1"),sQuery(id+"F0.wireOp",EDGE,"E11.8.0.3"),sQuery(id+"F0.wireOp",EDGE,"E11.9.0.0"),sQuery(id+"F0.wireOp",EDGE,"E11.9.0.3"),sQuery(id+"F0.wireOp",EDGE,"E11.2.0.2"),sQuery(id+"F0.wireOp",EDGE,"E11.3.0.2"),sQuery(id+"F0.wireOp",EDGE,"E11.4.0.2"),sQuery(id+"F0.wireOp",EDGE,"E11.5.0.2"),sQuery(id+"F0.wireOp",EDGE,"E11.6.0.2"),sQuery(id+"F0.wireOp",EDGE,"E11.7.0.2"),sQuery(id+"F0.wireOp",EDGE,"E11.8.0.2"),sQuery(id+"F0.wireOp",EDGE,"E11.9.0.2"),sQuery(id+"F0.wireOp",EDGE,"E13.0.2.2"),sQuery(id+"F0.wireOp",EDGE,"E13.0.3.1"),sQuery(id+"F0.wireOp",EDGE,"E13.0.3.2"),sQuery(id+"F0.wireOp",EDGE,"E13.0.3.3"),sQuery(id+"F0.wireOp",EDGE,"E13.0.4.1"),sQuery(id+"F0.wireOp",EDGE,"E13.0.4.2"),sQuery(id+"F0.wireOp",EDGE,"E13.0.4.3"),sQuery(id+"F0.wireOp",EDGE,"E14.trimOffspring"),sQuery(id+"F0.wireOp",EDGE,"E15.trimOffspring"),sQuery(id+"F0.wireOp",EDGE,"E16.trimOffspring"),sQuery(id+"F0.wireOp",EDGE,"E18.top"),sQuery(id+"F0.wireOp",EDGE,"E18.left"),sQuery(id+"F0.wireOp",EDGE,"E18.right"),sQuery(id+"F0.wireOp",EDGE,"E19.trimOffspring"),sQuery(id+"F0.wireOp",EDGE,"E20.1.0.0"),sQuery(id+"F0.wireOp",EDGE,"E20.1.0.1"),sQuery(id+"F0.wireOp",EDGE,"E20.1.0.2"),sQuery(id+"F0.wireOp",EDGE,"E20.2.0.0"),sQuery(id+"F0.wireOp",EDGE,"E20.2.0.1"),sQuery(id+"F0.wireOp",EDGE,"E20.2.0.2"),sQuery(id+"F0.wireOp",EDGE,"E20.3.0.0"),sQuery(id+"F0.wireOp",EDGE,"E20.3.0.1"),sQuery(id+"F0.wireOp",EDGE,"E20.3.0.2"),sQuery(id+"F0.wireOp",EDGE,"E20.4.0.0"),sQuery(id+"F0.wireOp",EDGE,"E20.4.0.1"),sQuery(id+"F0.wireOp",EDGE,"E20.4.0.2"),sQuery(id+"F0.wireOp",EDGE,"E21.trimOffspring"),sQuery(id+"F0.wireOp",EDGE,"E22.trimOffspring"),sQuery(id+"F0.wireOp",EDGE,"E23.trimOffspring")])]}),"instanceName":"1"});
            var Q2;
            Q2=makeQuery(id+"F8.opExtrude","SWEPT_BODY",BODY,{"disambiguationData":[OSD([sQuery(id+"F3.wireOp",EDGE,"E29.top"),sQuery(id+"F3.wireOp",EDGE,"E29.left"),sQuery(id+"F3.wireOp",EDGE,"E29.right"),sQuery(id+"F3.wireOp",EDGE,"E31.top"),sQuery(id+"F3.wireOp",EDGE,"E31.right"),sQuery(id+"F3.wireOp",EDGE,"E33.1.0.1"),sQuery(id+"F3.wireOp",EDGE,"E33.1.0.2"),sQuery(id+"F3.wireOp",EDGE,"E33.1.0.3"),sQuery(id+"F3.wireOp",EDGE,"E33.2.0.1"),sQuery(id+"F3.wireOp",EDGE,"E33.2.0.2"),sQuery(id+"F3.wireOp",EDGE,"E33.2.0.3"),sQuery(id+"F3.wireOp",EDGE,"E33.3.0.1"),sQuery(id+"F3.wireOp",EDGE,"E33.3.0.2"),sQuery(id+"F3.wireOp",EDGE,"E33.3.0.3"),sQuery(id+"F3.wireOp",EDGE,"E33.4.0.1"),sQuery(id+"F3.wireOp",EDGE,"E33.4.0.2"),sQuery(id+"F3.wireOp",EDGE,"E33.4.0.3"),sQuery(id+"F3.wireOp",EDGE,"E38.trimOffspring"),sQuery(id+"F3.wireOp",EDGE,"E39.trimOffspring"),sQuery(id+"F3.wireOp",EDGE,"E40.trimOffspring"),sQuery(id+"F3.wireOp",EDGE,"E41.trimOffspring"),sQuery(id+"F3.wireOp",EDGE,"E42")])]});
            booleanBodies(context, id + "F11", {"operationType" : BooleanOperationType.SUBTRACTION, "tools" : qUnion([Q0, Q1]), "targets" : qUnion([Q2]), "keepTools" : true});
        }
        {
            var Q0;
            Q0=qCreatedBy(makeId("Top.planeOp"),FACE);
            var sketch = newSketch(context, id + "F12", { "sketchPlane" : qUnion([Q0])});
            skLineSegment(sketch, "E43.bottom", {"start": v(-97, 200) * mm, "end": v(3, 200) * mm});
            skLineSegment(sketch, "E43.top", {"start": v(-97, 0) * mm, "end": v(3, 0) * mm});
            skLineSegment(sketch, "E43.left", {"start": v(-97, 200) * mm, "end": v(-97, 0) * mm});
            skLineSegment(sketch, "E43.right", {"start": v(3, 200) * mm, "end": v(3, 0) * mm});
            skLineSegment(sketch, "E44", {"start": v(-97, 100) * mm, "end": v(3, 100) * mm});
            skSolve(sketch);
        }
        {
            var Q0;
            {var subQ0=sQuery(id+"F12.wireOp",EDGE,"E43.top");Q0=makeQuery(id+"F12.imprint","IMPRINT",FACE,{"disambiguationData":[TD([[makeQuery(id+"F12.imprint","IMPRINT",EDGE,{"derivedFrom":subQ0}),1.0]])]});}
            extrude(context, id + "F13", {"entities" : qUnion([Q0]), "depth" : -3 * mm, "offsetDistance" : 25 * mm});
        }
        {
            var Q0;
            {var subQ0=sQuery(id+"F12.wireOp",EDGE,"E43.bottom");Q0=makeQuery(id+"F12.imprint","IMPRINT",FACE,{"disambiguationData":[TD([[makeQuery(id+"F12.imprint","IMPRINT",EDGE,{"derivedFrom":subQ0}),-1.0]])]});}
            extrude(context, id + "F14", {"entities" : qUnion([Q0]), "depth" : -3 * mm, "offsetDistance" : 25 * mm});
        }
        {
            var Q0;
            Q0=qSketchRegion(id+"F12",true);
            extrude(context, id + "F15", {"entities" : qUnion([Q0]), "oppositeDirection" : true, "depth" : 100 * mm, "offsetDistance" : 25 * mm, "hasSecondDirection" : true, "secondDirectionOppositeDirection" : true, "secondDirectionDepth" : 97 * mm});
        }
        {
            var Q0;
            Q0=makeQuery(id+"F6.opExtrude","SWEPT_BODY",BODY,{"disambiguationData":[OSD([sQuery(id+"F3.wireOp",EDGE,"E29.bottom"),sQuery(id+"F3.wireOp",EDGE,"E29.top"),sQuery(id+"F3.wireOp",EDGE,"E29.left"),sQuery(id+"F3.wireOp",EDGE,"E29.right"),sQuery(id+"F3.wireOp",EDGE,"E30.top"),sQuery(id+"F3.wireOp",EDGE,"E30.right"),sQuery(id+"F3.wireOp",EDGE,"E31.top"),sQuery(id+"F3.wireOp",EDGE,"E31.right"),sQuery(id+"F3.wireOp",EDGE,"E32.1.0.0"),sQuery(id+"F3.wireOp",EDGE,"E32.1.0.1"),sQuery(id+"F3.wireOp",EDGE,"E32.1.0.2"),sQuery(id+"F3.wireOp",EDGE,"E32.2.0.0"),sQuery(id+"F3.wireOp",EDGE,"E32.2.0.1"),sQuery(id+"F3.wireOp",EDGE,"E32.2.0.2"),sQuery(id+"F3.wireOp",EDGE,"E32.3.0.0"),sQuery(id+"F3.wireOp",EDGE,"E32.3.0.1"),sQuery(id+"F3.wireOp",EDGE,"E32.3.0.2"),sQuery(id+"F3.wireOp",EDGE,"E32.4.0.0"),sQuery(id+"F3.wireOp",EDGE,"E32.4.0.1"),sQuery(id+"F3.wireOp",EDGE,"E32.4.0.2"),sQuery(id+"F3.wireOp",EDGE,"E33.1.0.1"),sQuery(id+"F3.wireOp",EDGE,"E33.1.0.2"),sQuery(id+"F3.wireOp",EDGE,"E33.1.0.3"),sQuery(id+"F3.wireOp",EDGE,"E33.2.0.1"),sQuery(id+"F3.wireOp",EDGE,"E33.2.0.2"),sQuery(id+"F3.wireOp",EDGE,"E33.2.0.3"),sQuery(id+"F3.wireOp",EDGE,"E33.3.0.1"),sQuery(id+"F3.wireOp",EDGE,"E33.3.0.2"),sQuery(id+"F3.wireOp",EDGE,"E33.3.0.3"),sQuery(id+"F3.wireOp",EDGE,"E33.4.0.1"),sQuery(id+"F3.wireOp",EDGE,"E33.4.0.2"),sQuery(id+"F3.wireOp",EDGE,"E33.4.0.3"),sQuery(id+"F3.wireOp",EDGE,"E34.trimOffspring"),sQuery(id+"F3.wireOp",EDGE,"E35.trimOffspring"),sQuery(id+"F3.wireOp",EDGE,"E36.trimOffspring"),sQuery(id+"F3.wireOp",EDGE,"E37.trimOffspring"),sQuery(id+"F3.wireOp",EDGE,"E38.trimOffspring"),sQuery(id+"F3.wireOp",EDGE,"E39.trimOffspring"),sQuery(id+"F3.wireOp",EDGE,"E40.trimOffspring"),sQuery(id+"F3.wireOp",EDGE,"E41.trimOffspring")])]});
            var Q1;
            Q1=makeQuery(id+"F1.opExtrude","SWEPT_BODY",BODY,{"disambiguationData":[OSD([sQuery(id+"F0.wireOp",EDGE,"E0.bottom"),sQuery(id+"F0.wireOp",EDGE,"E0.top"),sQuery(id+"F0.wireOp",EDGE,"E0.left"),sQuery(id+"F0.wireOp",EDGE,"E1"),sQuery(id+"F0.wireOp",EDGE,"E2"),sQuery(id+"F0.wireOp",EDGE,"E3.bottom"),sQuery(id+"F0.wireOp",EDGE,"E3.top"),sQuery(id+"F0.wireOp",EDGE,"E3.right"),sQuery(id+"F0.wireOp",EDGE,"E4.trimOffspring"),sQuery(id+"F0.wireOp",EDGE,"E5.0.1.0"),sQuery(id+"F0.wireOp",EDGE,"E5.0.1.1"),sQuery(id+"F0.wireOp",EDGE,"E5.0.1.2"),sQuery(id+"F0.wireOp",EDGE,"E5.0.2.0"),sQuery(id+"F0.wireOp",EDGE,"E5.0.2.1"),sQuery(id+"F0.wireOp",EDGE,"E5.0.2.2"),sQuery(id+"F0.wireOp",EDGE,"E5.0.3.0"),sQuery(id+"F0.wireOp",EDGE,"E5.0.3.1"),sQuery(id+"F0.wireOp",EDGE,"E5.0.3.2"),sQuery(id+"F0.wireOp",EDGE,"E5.0.4.0"),sQuery(id+"F0.wireOp",EDGE,"E5.0.4.1"),sQuery(id+"F0.wireOp",EDGE,"E6.trimOffspring"),sQuery(id+"F0.wireOp",EDGE,"E7.trimOffspring"),sQuery(id+"F0.wireOp",EDGE,"E8.trimOffspring"),sQuery(id+"F0.wireOp",EDGE,"E9.top"),sQuery(id+"F0.wireOp",EDGE,"E9.left"),sQuery(id+"F0.wireOp",EDGE,"E9.right"),sQuery(id+"F0.wireOp",EDGE,"E11.1.0.0"),sQuery(id+"F0.wireOp",EDGE,"E11.1.0.1"),sQuery(id+"F0.wireOp",EDGE,"E10.trimOffspring"),sQuery(id+"F0.wireOp",EDGE,"E11.1.0.3"),sQuery(id+"F0.wireOp",EDGE,"E11.2.0.0"),sQuery(id+"F0.wireOp",EDGE,"E11.2.0.1"),sQuery(id+"F0.wireOp",EDGE,"E11.2.0.3"),sQuery(id+"F0.wireOp",EDGE,"E11.3.0.0"),sQuery(id+"F0.wireOp",EDGE,"E11.3.0.1"),sQuery(id+"F0.wireOp",EDGE,"E11.3.0.3"),sQuery(id+"F0.wireOp",EDGE,"E11.4.0.0"),sQuery(id+"F0.wireOp",EDGE,"E11.4.0.1"),sQuery(id+"F0.wireOp",EDGE,"E11.4.0.3"),sQuery(id+"F0.wireOp",EDGE,"E11.5.0.0"),sQuery(id+"F0.wireOp",EDGE,"E11.5.0.1"),sQuery(id+"F0.wireOp",EDGE,"E11.5.0.3"),sQuery(id+"F0.wireOp",EDGE,"E11.6.0.0"),sQuery(id+"F0.wireOp",EDGE,"E11.6.0.1"),sQuery(id+"F0.wireOp",EDGE,"E11.6.0.3"),sQuery(id+"F0.wireOp",EDGE,"E11.7.0.0"),sQuery(id+"F0.wireOp",EDGE,"E11.7.0.1"),sQuery(id+"F0.wireOp",EDGE,"E11.7.0.3"),sQuery(id+"F0.wireOp",EDGE,"E11.8.0.0"),sQuery(id+"F0.wireOp",EDGE,"E11.8.0.1"),sQuery(id+"F0.wireOp",EDGE,"E11.8.0.3"),sQuery(id+"F0.wireOp",EDGE,"E11.9.0.0"),sQuery(id+"F0.wireOp",EDGE,"E11.9.0.3"),sQuery(id+"F0.wireOp",EDGE,"E11.2.0.2"),sQuery(id+"F0.wireOp",EDGE,"E11.3.0.2"),sQuery(id+"F0.wireOp",EDGE,"E11.4.0.2"),sQuery(id+"F0.wireOp",EDGE,"E11.5.0.2"),sQuery(id+"F0.wireOp",EDGE,"E11.6.0.2"),sQuery(id+"F0.wireOp",EDGE,"E11.7.0.2"),sQuery(id+"F0.wireOp",EDGE,"E11.8.0.2"),sQuery(id+"F0.wireOp",EDGE,"E11.9.0.2"),sQuery(id+"F0.wireOp",EDGE,"E13.0.2.2"),sQuery(id+"F0.wireOp",EDGE,"E13.0.3.1"),sQuery(id+"F0.wireOp",EDGE,"E13.0.3.2"),sQuery(id+"F0.wireOp",EDGE,"E13.0.3.3"),sQuery(id+"F0.wireOp",EDGE,"E13.0.4.1"),sQuery(id+"F0.wireOp",EDGE,"E13.0.4.2"),sQuery(id+"F0.wireOp",EDGE,"E13.0.4.3"),sQuery(id+"F0.wireOp",EDGE,"E14.trimOffspring"),sQuery(id+"F0.wireOp",EDGE,"E15.trimOffspring"),sQuery(id+"F0.wireOp",EDGE,"E16.trimOffspring"),sQuery(id+"F0.wireOp",EDGE,"E18.top"),sQuery(id+"F0.wireOp",EDGE,"E18.left"),sQuery(id+"F0.wireOp",EDGE,"E18.right"),sQuery(id+"F0.wireOp",EDGE,"E19.trimOffspring"),sQuery(id+"F0.wireOp",EDGE,"E20.1.0.0"),sQuery(id+"F0.wireOp",EDGE,"E20.1.0.1"),sQuery(id+"F0.wireOp",EDGE,"E20.1.0.2"),sQuery(id+"F0.wireOp",EDGE,"E20.2.0.0"),sQuery(id+"F0.wireOp",EDGE,"E20.2.0.1"),sQuery(id+"F0.wireOp",EDGE,"E20.2.0.2"),sQuery(id+"F0.wireOp",EDGE,"E20.3.0.0"),sQuery(id+"F0.wireOp",EDGE,"E20.3.0.1"),sQuery(id+"F0.wireOp",EDGE,"E20.3.0.2"),sQuery(id+"F0.wireOp",EDGE,"E20.4.0.0"),sQuery(id+"F0.wireOp",EDGE,"E20.4.0.1"),sQuery(id+"F0.wireOp",EDGE,"E20.4.0.2"),sQuery(id+"F0.wireOp",EDGE,"E21.trimOffspring"),sQuery(id+"F0.wireOp",EDGE,"E22.trimOffspring"),sQuery(id+"F0.wireOp",EDGE,"E23.trimOffspring")])]});
            var Q2;
            Q2=makeQuery(id+"F8.opExtrude","SWEPT_BODY",BODY,{"disambiguationData":[OSD([sQuery(id+"F3.wireOp",EDGE,"E29.top"),sQuery(id+"F3.wireOp",EDGE,"E29.left"),sQuery(id+"F3.wireOp",EDGE,"E29.right"),sQuery(id+"F3.wireOp",EDGE,"E31.top"),sQuery(id+"F3.wireOp",EDGE,"E31.right"),sQuery(id+"F3.wireOp",EDGE,"E33.1.0.1"),sQuery(id+"F3.wireOp",EDGE,"E33.1.0.2"),sQuery(id+"F3.wireOp",EDGE,"E33.1.0.3"),sQuery(id+"F3.wireOp",EDGE,"E33.2.0.1"),sQuery(id+"F3.wireOp",EDGE,"E33.2.0.2"),sQuery(id+"F3.wireOp",EDGE,"E33.2.0.3"),sQuery(id+"F3.wireOp",EDGE,"E33.3.0.1"),sQuery(id+"F3.wireOp",EDGE,"E33.3.0.2"),sQuery(id+"F3.wireOp",EDGE,"E33.3.0.3"),sQuery(id+"F3.wireOp",EDGE,"E33.4.0.1"),sQuery(id+"F3.wireOp",EDGE,"E33.4.0.2"),sQuery(id+"F3.wireOp",EDGE,"E33.4.0.3"),sQuery(id+"F3.wireOp",EDGE,"E38.trimOffspring"),sQuery(id+"F3.wireOp",EDGE,"E39.trimOffspring"),sQuery(id+"F3.wireOp",EDGE,"E40.trimOffspring"),sQuery(id+"F3.wireOp",EDGE,"E41.trimOffspring"),sQuery(id+"F3.wireOp",EDGE,"E42")])]});
            var Q3;
            Q3=makeQuery(id+"F4.opPattern","COPY",BODY,{"derivedFrom":makeQuery(id+"F1.opExtrude","SWEPT_BODY",BODY,{"disambiguationData":[OSD([sQuery(id+"F0.wireOp",EDGE,"E0.bottom"),sQuery(id+"F0.wireOp",EDGE,"E0.top"),sQuery(id+"F0.wireOp",EDGE,"E0.left"),sQuery(id+"F0.wireOp",EDGE,"E1"),sQuery(id+"F0.wireOp",EDGE,"E2"),sQuery(id+"F0.wireOp",EDGE,"E3.bottom"),sQuery(id+"F0.wireOp",EDGE,"E3.top"),sQuery(id+"F0.wireOp",EDGE,"E3.right"),sQuery(id+"F0.wireOp",EDGE,"E4.trimOffspring"),sQuery(id+"F0.wireOp",EDGE,"E5.0.1.0"),sQuery(id+"F0.wireOp",EDGE,"E5.0.1.1"),sQuery(id+"F0.wireOp",EDGE,"E5.0.1.2"),sQuery(id+"F0.wireOp",EDGE,"E5.0.2.0"),sQuery(id+"F0.wireOp",EDGE,"E5.0.2.1"),sQuery(id+"F0.wireOp",EDGE,"E5.0.2.2"),sQuery(id+"F0.wireOp",EDGE,"E5.0.3.0"),sQuery(id+"F0.wireOp",EDGE,"E5.0.3.1"),sQuery(id+"F0.wireOp",EDGE,"E5.0.3.2"),sQuery(id+"F0.wireOp",EDGE,"E5.0.4.0"),sQuery(id+"F0.wireOp",EDGE,"E5.0.4.1"),sQuery(id+"F0.wireOp",EDGE,"E6.trimOffspring"),sQuery(id+"F0.wireOp",EDGE,"E7.trimOffspring"),sQuery(id+"F0.wireOp",EDGE,"E8.trimOffspring"),sQuery(id+"F0.wireOp",EDGE,"E9.top"),sQuery(id+"F0.wireOp",EDGE,"E9.left"),sQuery(id+"F0.wireOp",EDGE,"E9.right"),sQuery(id+"F0.wireOp",EDGE,"E11.1.0.0"),sQuery(id+"F0.wireOp",EDGE,"E11.1.0.1"),sQuery(id+"F0.wireOp",EDGE,"E10.trimOffspring"),sQuery(id+"F0.wireOp",EDGE,"E11.1.0.3"),sQuery(id+"F0.wireOp",EDGE,"E11.2.0.0"),sQuery(id+"F0.wireOp",EDGE,"E11.2.0.1"),sQuery(id+"F0.wireOp",EDGE,"E11.2.0.3"),sQuery(id+"F0.wireOp",EDGE,"E11.3.0.0"),sQuery(id+"F0.wireOp",EDGE,"E11.3.0.1"),sQuery(id+"F0.wireOp",EDGE,"E11.3.0.3"),sQuery(id+"F0.wireOp",EDGE,"E11.4.0.0"),sQuery(id+"F0.wireOp",EDGE,"E11.4.0.1"),sQuery(id+"F0.wireOp",EDGE,"E11.4.0.3"),sQuery(id+"F0.wireOp",EDGE,"E11.5.0.0"),sQuery(id+"F0.wireOp",EDGE,"E11.5.0.1"),sQuery(id+"F0.wireOp",EDGE,"E11.5.0.3"),sQuery(id+"F0.wireOp",EDGE,"E11.6.0.0"),sQuery(id+"F0.wireOp",EDGE,"E11.6.0.1"),sQuery(id+"F0.wireOp",EDGE,"E11.6.0.3"),sQuery(id+"F0.wireOp",EDGE,"E11.7.0.0"),sQuery(id+"F0.wireOp",EDGE,"E11.7.0.1"),sQuery(id+"F0.wireOp",EDGE,"E11.7.0.3"),sQuery(id+"F0.wireOp",EDGE,"E11.8.0.0"),sQuery(id+"F0.wireOp",EDGE,"E11.8.0.1"),sQuery(id+"F0.wireOp",EDGE,"E11.8.0.3"),sQuery(id+"F0.wireOp",EDGE,"E11.9.0.0"),sQuery(id+"F0.wireOp",EDGE,"E11.9.0.3"),sQuery(id+"F0.wireOp",EDGE,"E11.2.0.2"),sQuery(id+"F0.wireOp",EDGE,"E11.3.0.2"),sQuery(id+"F0.wireOp",EDGE,"E11.4.0.2"),sQuery(id+"F0.wireOp",EDGE,"E11.5.0.2"),sQuery(id+"F0.wireOp",EDGE,"E11.6.0.2"),sQuery(id+"F0.wireOp",EDGE,"E11.7.0.2"),sQuery(id+"F0.wireOp",EDGE,"E11.8.0.2"),sQuery(id+"F0.wireOp",EDGE,"E11.9.0.2"),sQuery(id+"F0.wireOp",EDGE,"E13.0.2.2"),sQuery(id+"F0.wireOp",EDGE,"E13.0.3.1"),sQuery(id+"F0.wireOp",EDGE,"E13.0.3.2"),sQuery(id+"F0.wireOp",EDGE,"E13.0.3.3"),sQuery(id+"F0.wireOp",EDGE,"E13.0.4.1"),sQuery(id+"F0.wireOp",EDGE,"E13.0.4.2"),sQuery(id+"F0.wireOp",EDGE,"E13.0.4.3"),sQuery(id+"F0.wireOp",EDGE,"E14.trimOffspring"),sQuery(id+"F0.wireOp",EDGE,"E15.trimOffspring"),sQuery(id+"F0.wireOp",EDGE,"E16.trimOffspring"),sQuery(id+"F0.wireOp",EDGE,"E18.top"),sQuery(id+"F0.wireOp",EDGE,"E18.left"),sQuery(id+"F0.wireOp",EDGE,"E18.right"),sQuery(id+"F0.wireOp",EDGE,"E19.trimOffspring"),sQuery(id+"F0.wireOp",EDGE,"E20.1.0.0"),sQuery(id+"F0.wireOp",EDGE,"E20.1.0.1"),sQuery(id+"F0.wireOp",EDGE,"E20.1.0.2"),sQuery(id+"F0.wireOp",EDGE,"E20.2.0.0"),sQuery(id+"F0.wireOp",EDGE,"E20.2.0.1"),sQuery(id+"F0.wireOp",EDGE,"E20.2.0.2"),sQuery(id+"F0.wireOp",EDGE,"E20.3.0.0"),sQuery(id+"F0.wireOp",EDGE,"E20.3.0.1"),sQuery(id+"F0.wireOp",EDGE,"E20.3.0.2"),sQuery(id+"F0.wireOp",EDGE,"E20.4.0.0"),sQuery(id+"F0.wireOp",EDGE,"E20.4.0.1"),sQuery(id+"F0.wireOp",EDGE,"E20.4.0.2"),sQuery(id+"F0.wireOp",EDGE,"E21.trimOffspring"),sQuery(id+"F0.wireOp",EDGE,"E22.trimOffspring"),sQuery(id+"F0.wireOp",EDGE,"E23.trimOffspring")])]}),"instanceName":"1"});
            var Q4;
            Q4=makeQuery(id+"F15.opExtrude","SWEPT_BODY",BODY,{"disambiguationData":[OSD([sQuery(id+"F12.wireOp",EDGE,"E43.bottom"),sQuery(id+"F12.wireOp",EDGE,"E43.top"),sQuery(id+"F12.wireOp",EDGE,"E43.left"),sQuery(id+"F12.wireOp",EDGE,"E43.right")])]});
            booleanBodies(context, id + "F16", {"operationType" : BooleanOperationType.SUBTRACTION, "tools" : qUnion([Q0, Q1, Q2, Q3]), "targets" : qUnion([Q4]), "keepTools" : true});
        }
        {
            var Q0;
            Q0=makeQuery(id+"F6.opExtrude","SWEPT_BODY",BODY,{"disambiguationData":[OSD([sQuery(id+"F3.wireOp",EDGE,"E29.bottom"),sQuery(id+"F3.wireOp",EDGE,"E29.top"),sQuery(id+"F3.wireOp",EDGE,"E29.left"),sQuery(id+"F3.wireOp",EDGE,"E29.right"),sQuery(id+"F3.wireOp",EDGE,"E30.top"),sQuery(id+"F3.wireOp",EDGE,"E30.right"),sQuery(id+"F3.wireOp",EDGE,"E31.top"),sQuery(id+"F3.wireOp",EDGE,"E31.right"),sQuery(id+"F3.wireOp",EDGE,"E32.1.0.0"),sQuery(id+"F3.wireOp",EDGE,"E32.1.0.1"),sQuery(id+"F3.wireOp",EDGE,"E32.1.0.2"),sQuery(id+"F3.wireOp",EDGE,"E32.2.0.0"),sQuery(id+"F3.wireOp",EDGE,"E32.2.0.1"),sQuery(id+"F3.wireOp",EDGE,"E32.2.0.2"),sQuery(id+"F3.wireOp",EDGE,"E32.3.0.0"),sQuery(id+"F3.wireOp",EDGE,"E32.3.0.1"),sQuery(id+"F3.wireOp",EDGE,"E32.3.0.2"),sQuery(id+"F3.wireOp",EDGE,"E32.4.0.0"),sQuery(id+"F3.wireOp",EDGE,"E32.4.0.1"),sQuery(id+"F3.wireOp",EDGE,"E32.4.0.2"),sQuery(id+"F3.wireOp",EDGE,"E33.1.0.1"),sQuery(id+"F3.wireOp",EDGE,"E33.1.0.2"),sQuery(id+"F3.wireOp",EDGE,"E33.1.0.3"),sQuery(id+"F3.wireOp",EDGE,"E33.2.0.1"),sQuery(id+"F3.wireOp",EDGE,"E33.2.0.2"),sQuery(id+"F3.wireOp",EDGE,"E33.2.0.3"),sQuery(id+"F3.wireOp",EDGE,"E33.3.0.1"),sQuery(id+"F3.wireOp",EDGE,"E33.3.0.2"),sQuery(id+"F3.wireOp",EDGE,"E33.3.0.3"),sQuery(id+"F3.wireOp",EDGE,"E33.4.0.1"),sQuery(id+"F3.wireOp",EDGE,"E33.4.0.2"),sQuery(id+"F3.wireOp",EDGE,"E33.4.0.3"),sQuery(id+"F3.wireOp",EDGE,"E34.trimOffspring"),sQuery(id+"F3.wireOp",EDGE,"E35.trimOffspring"),sQuery(id+"F3.wireOp",EDGE,"E36.trimOffspring"),sQuery(id+"F3.wireOp",EDGE,"E37.trimOffspring"),sQuery(id+"F3.wireOp",EDGE,"E38.trimOffspring"),sQuery(id+"F3.wireOp",EDGE,"E39.trimOffspring"),sQuery(id+"F3.wireOp",EDGE,"E40.trimOffspring"),sQuery(id+"F3.wireOp",EDGE,"E41.trimOffspring")])]});
            var Q1;
            Q1=makeQuery(id+"F1.opExtrude","SWEPT_BODY",BODY,{"disambiguationData":[OSD([sQuery(id+"F0.wireOp",EDGE,"E0.bottom"),sQuery(id+"F0.wireOp",EDGE,"E0.top"),sQuery(id+"F0.wireOp",EDGE,"E0.left"),sQuery(id+"F0.wireOp",EDGE,"E1"),sQuery(id+"F0.wireOp",EDGE,"E2"),sQuery(id+"F0.wireOp",EDGE,"E3.bottom"),sQuery(id+"F0.wireOp",EDGE,"E3.top"),sQuery(id+"F0.wireOp",EDGE,"E3.right"),sQuery(id+"F0.wireOp",EDGE,"E4.trimOffspring"),sQuery(id+"F0.wireOp",EDGE,"E5.0.1.0"),sQuery(id+"F0.wireOp",EDGE,"E5.0.1.1"),sQuery(id+"F0.wireOp",EDGE,"E5.0.1.2"),sQuery(id+"F0.wireOp",EDGE,"E5.0.2.0"),sQuery(id+"F0.wireOp",EDGE,"E5.0.2.1"),sQuery(id+"F0.wireOp",EDGE,"E5.0.2.2"),sQuery(id+"F0.wireOp",EDGE,"E5.0.3.0"),sQuery(id+"F0.wireOp",EDGE,"E5.0.3.1"),sQuery(id+"F0.wireOp",EDGE,"E5.0.3.2"),sQuery(id+"F0.wireOp",EDGE,"E5.0.4.0"),sQuery(id+"F0.wireOp",EDGE,"E5.0.4.1"),sQuery(id+"F0.wireOp",EDGE,"E6.trimOffspring"),sQuery(id+"F0.wireOp",EDGE,"E7.trimOffspring"),sQuery(id+"F0.wireOp",EDGE,"E8.trimOffspring"),sQuery(id+"F0.wireOp",EDGE,"E9.top"),sQuery(id+"F0.wireOp",EDGE,"E9.left"),sQuery(id+"F0.wireOp",EDGE,"E9.right"),sQuery(id+"F0.wireOp",EDGE,"E11.1.0.0"),sQuery(id+"F0.wireOp",EDGE,"E11.1.0.1"),sQuery(id+"F0.wireOp",EDGE,"E10.trimOffspring"),sQuery(id+"F0.wireOp",EDGE,"E11.1.0.3"),sQuery(id+"F0.wireOp",EDGE,"E11.2.0.0"),sQuery(id+"F0.wireOp",EDGE,"E11.2.0.1"),sQuery(id+"F0.wireOp",EDGE,"E11.2.0.3"),sQuery(id+"F0.wireOp",EDGE,"E11.3.0.0"),sQuery(id+"F0.wireOp",EDGE,"E11.3.0.1"),sQuery(id+"F0.wireOp",EDGE,"E11.3.0.3"),sQuery(id+"F0.wireOp",EDGE,"E11.4.0.0"),sQuery(id+"F0.wireOp",EDGE,"E11.4.0.1"),sQuery(id+"F0.wireOp",EDGE,"E11.4.0.3"),sQuery(id+"F0.wireOp",EDGE,"E11.5.0.0"),sQuery(id+"F0.wireOp",EDGE,"E11.5.0.1"),sQuery(id+"F0.wireOp",EDGE,"E11.5.0.3"),sQuery(id+"F0.wireOp",EDGE,"E11.6.0.0"),sQuery(id+"F0.wireOp",EDGE,"E11.6.0.1"),sQuery(id+"F0.wireOp",EDGE,"E11.6.0.3"),sQuery(id+"F0.wireOp",EDGE,"E11.7.0.0"),sQuery(id+"F0.wireOp",EDGE,"E11.7.0.1"),sQuery(id+"F0.wireOp",EDGE,"E11.7.0.3"),sQuery(id+"F0.wireOp",EDGE,"E11.8.0.0"),sQuery(id+"F0.wireOp",EDGE,"E11.8.0.1"),sQuery(id+"F0.wireOp",EDGE,"E11.8.0.3"),sQuery(id+"F0.wireOp",EDGE,"E11.9.0.0"),sQuery(id+"F0.wireOp",EDGE,"E11.9.0.3"),sQuery(id+"F0.wireOp",EDGE,"E11.2.0.2"),sQuery(id+"F0.wireOp",EDGE,"E11.3.0.2"),sQuery(id+"F0.wireOp",EDGE,"E11.4.0.2"),sQuery(id+"F0.wireOp",EDGE,"E11.5.0.2"),sQuery(id+"F0.wireOp",EDGE,"E11.6.0.2"),sQuery(id+"F0.wireOp",EDGE,"E11.7.0.2"),sQuery(id+"F0.wireOp",EDGE,"E11.8.0.2"),sQuery(id+"F0.wireOp",EDGE,"E11.9.0.2"),sQuery(id+"F0.wireOp",EDGE,"E13.0.2.2"),sQuery(id+"F0.wireOp",EDGE,"E13.0.3.1"),sQuery(id+"F0.wireOp",EDGE,"E13.0.3.2"),sQuery(id+"F0.wireOp",EDGE,"E13.0.3.3"),sQuery(id+"F0.wireOp",EDGE,"E13.0.4.1"),sQuery(id+"F0.wireOp",EDGE,"E13.0.4.2"),sQuery(id+"F0.wireOp",EDGE,"E13.0.4.3"),sQuery(id+"F0.wireOp",EDGE,"E14.trimOffspring"),sQuery(id+"F0.wireOp",EDGE,"E15.trimOffspring"),sQuery(id+"F0.wireOp",EDGE,"E16.trimOffspring"),sQuery(id+"F0.wireOp",EDGE,"E18.top"),sQuery(id+"F0.wireOp",EDGE,"E18.left"),sQuery(id+"F0.wireOp",EDGE,"E18.right"),sQuery(id+"F0.wireOp",EDGE,"E19.trimOffspring"),sQuery(id+"F0.wireOp",EDGE,"E20.1.0.0"),sQuery(id+"F0.wireOp",EDGE,"E20.1.0.1"),sQuery(id+"F0.wireOp",EDGE,"E20.1.0.2"),sQuery(id+"F0.wireOp",EDGE,"E20.2.0.0"),sQuery(id+"F0.wireOp",EDGE,"E20.2.0.1"),sQuery(id+"F0.wireOp",EDGE,"E20.2.0.2"),sQuery(id+"F0.wireOp",EDGE,"E20.3.0.0"),sQuery(id+"F0.wireOp",EDGE,"E20.3.0.1"),sQuery(id+"F0.wireOp",EDGE,"E20.3.0.2"),sQuery(id+"F0.wireOp",EDGE,"E20.4.0.0"),sQuery(id+"F0.wireOp",EDGE,"E20.4.0.1"),sQuery(id+"F0.wireOp",EDGE,"E20.4.0.2"),sQuery(id+"F0.wireOp",EDGE,"E21.trimOffspring"),sQuery(id+"F0.wireOp",EDGE,"E22.trimOffspring"),sQuery(id+"F0.wireOp",EDGE,"E23.trimOffspring")])]});
            var Q2;
            Q2=makeQuery(id+"F4.opPattern","COPY",BODY,{"derivedFrom":makeQuery(id+"F1.opExtrude","SWEPT_BODY",BODY,{"disambiguationData":[OSD([sQuery(id+"F0.wireOp",EDGE,"E0.bottom"),sQuery(id+"F0.wireOp",EDGE,"E0.top"),sQuery(id+"F0.wireOp",EDGE,"E0.left"),sQuery(id+"F0.wireOp",EDGE,"E1"),sQuery(id+"F0.wireOp",EDGE,"E2"),sQuery(id+"F0.wireOp",EDGE,"E3.bottom"),sQuery(id+"F0.wireOp",EDGE,"E3.top"),sQuery(id+"F0.wireOp",EDGE,"E3.right"),sQuery(id+"F0.wireOp",EDGE,"E4.trimOffspring"),sQuery(id+"F0.wireOp",EDGE,"E5.0.1.0"),sQuery(id+"F0.wireOp",EDGE,"E5.0.1.1"),sQuery(id+"F0.wireOp",EDGE,"E5.0.1.2"),sQuery(id+"F0.wireOp",EDGE,"E5.0.2.0"),sQuery(id+"F0.wireOp",EDGE,"E5.0.2.1"),sQuery(id+"F0.wireOp",EDGE,"E5.0.2.2"),sQuery(id+"F0.wireOp",EDGE,"E5.0.3.0"),sQuery(id+"F0.wireOp",EDGE,"E5.0.3.1"),sQuery(id+"F0.wireOp",EDGE,"E5.0.3.2"),sQuery(id+"F0.wireOp",EDGE,"E5.0.4.0"),sQuery(id+"F0.wireOp",EDGE,"E5.0.4.1"),sQuery(id+"F0.wireOp",EDGE,"E6.trimOffspring"),sQuery(id+"F0.wireOp",EDGE,"E7.trimOffspring"),sQuery(id+"F0.wireOp",EDGE,"E8.trimOffspring"),sQuery(id+"F0.wireOp",EDGE,"E9.top"),sQuery(id+"F0.wireOp",EDGE,"E9.left"),sQuery(id+"F0.wireOp",EDGE,"E9.right"),sQuery(id+"F0.wireOp",EDGE,"E11.1.0.0"),sQuery(id+"F0.wireOp",EDGE,"E11.1.0.1"),sQuery(id+"F0.wireOp",EDGE,"E10.trimOffspring"),sQuery(id+"F0.wireOp",EDGE,"E11.1.0.3"),sQuery(id+"F0.wireOp",EDGE,"E11.2.0.0"),sQuery(id+"F0.wireOp",EDGE,"E11.2.0.1"),sQuery(id+"F0.wireOp",EDGE,"E11.2.0.3"),sQuery(id+"F0.wireOp",EDGE,"E11.3.0.0"),sQuery(id+"F0.wireOp",EDGE,"E11.3.0.1"),sQuery(id+"F0.wireOp",EDGE,"E11.3.0.3"),sQuery(id+"F0.wireOp",EDGE,"E11.4.0.0"),sQuery(id+"F0.wireOp",EDGE,"E11.4.0.1"),sQuery(id+"F0.wireOp",EDGE,"E11.4.0.3"),sQuery(id+"F0.wireOp",EDGE,"E11.5.0.0"),sQuery(id+"F0.wireOp",EDGE,"E11.5.0.1"),sQuery(id+"F0.wireOp",EDGE,"E11.5.0.3"),sQuery(id+"F0.wireOp",EDGE,"E11.6.0.0"),sQuery(id+"F0.wireOp",EDGE,"E11.6.0.1"),sQuery(id+"F0.wireOp",EDGE,"E11.6.0.3"),sQuery(id+"F0.wireOp",EDGE,"E11.7.0.0"),sQuery(id+"F0.wireOp",EDGE,"E11.7.0.1"),sQuery(id+"F0.wireOp",EDGE,"E11.7.0.3"),sQuery(id+"F0.wireOp",EDGE,"E11.8.0.0"),sQuery(id+"F0.wireOp",EDGE,"E11.8.0.1"),sQuery(id+"F0.wireOp",EDGE,"E11.8.0.3"),sQuery(id+"F0.wireOp",EDGE,"E11.9.0.0"),sQuery(id+"F0.wireOp",EDGE,"E11.9.0.3"),sQuery(id+"F0.wireOp",EDGE,"E11.2.0.2"),sQuery(id+"F0.wireOp",EDGE,"E11.3.0.2"),sQuery(id+"F0.wireOp",EDGE,"E11.4.0.2"),sQuery(id+"F0.wireOp",EDGE,"E11.5.0.2"),sQuery(id+"F0.wireOp",EDGE,"E11.6.0.2"),sQuery(id+"F0.wireOp",EDGE,"E11.7.0.2"),sQuery(id+"F0.wireOp",EDGE,"E11.8.0.2"),sQuery(id+"F0.wireOp",EDGE,"E11.9.0.2"),sQuery(id+"F0.wireOp",EDGE,"E13.0.2.2"),sQuery(id+"F0.wireOp",EDGE,"E13.0.3.1"),sQuery(id+"F0.wireOp",EDGE,"E13.0.3.2"),sQuery(id+"F0.wireOp",EDGE,"E13.0.3.3"),sQuery(id+"F0.wireOp",EDGE,"E13.0.4.1"),sQuery(id+"F0.wireOp",EDGE,"E13.0.4.2"),sQuery(id+"F0.wireOp",EDGE,"E13.0.4.3"),sQuery(id+"F0.wireOp",EDGE,"E14.trimOffspring"),sQuery(id+"F0.wireOp",EDGE,"E15.trimOffspring"),sQuery(id+"F0.wireOp",EDGE,"E16.trimOffspring"),sQuery(id+"F0.wireOp",EDGE,"E18.top"),sQuery(id+"F0.wireOp",EDGE,"E18.left"),sQuery(id+"F0.wireOp",EDGE,"E18.right"),sQuery(id+"F0.wireOp",EDGE,"E19.trimOffspring"),sQuery(id+"F0.wireOp",EDGE,"E20.1.0.0"),sQuery(id+"F0.wireOp",EDGE,"E20.1.0.1"),sQuery(id+"F0.wireOp",EDGE,"E20.1.0.2"),sQuery(id+"F0.wireOp",EDGE,"E20.2.0.0"),sQuery(id+"F0.wireOp",EDGE,"E20.2.0.1"),sQuery(id+"F0.wireOp",EDGE,"E20.2.0.2"),sQuery(id+"F0.wireOp",EDGE,"E20.3.0.0"),sQuery(id+"F0.wireOp",EDGE,"E20.3.0.1"),sQuery(id+"F0.wireOp",EDGE,"E20.3.0.2"),sQuery(id+"F0.wireOp",EDGE,"E20.4.0.0"),sQuery(id+"F0.wireOp",EDGE,"E20.4.0.1"),sQuery(id+"F0.wireOp",EDGE,"E20.4.0.2"),sQuery(id+"F0.wireOp",EDGE,"E21.trimOffspring"),sQuery(id+"F0.wireOp",EDGE,"E22.trimOffspring"),sQuery(id+"F0.wireOp",EDGE,"E23.trimOffspring")])]}),"instanceName":"1"});
            var Q3;
            Q3=makeQuery(id+"F13.opExtrude","SWEPT_BODY",BODY,{"disambiguationData":[OSD([sQuery(id+"F12.wireOp",EDGE,"E43.top"),sQuery(id+"F12.wireOp",EDGE,"E43.left"),sQuery(id+"F12.wireOp",EDGE,"E43.right"),sQuery(id+"F12.wireOp",EDGE,"E44")])]});
            booleanBodies(context, id + "F17", {"operationType" : BooleanOperationType.SUBTRACTION, "tools" : qUnion([Q0, Q1, Q2]), "targets" : qUnion([Q3]), "keepTools" : true});
        }
        {
            var Q0;
            Q0=makeQuery(id+"F2.opExtrude","SWEPT_BODY",BODY,{"disambiguationData":[OSD([sQuery(id+"F0.wireOp",EDGE,"E0.right"),sQuery(id+"F0.wireOp",EDGE,"E1"),sQuery(id+"F0.wireOp",EDGE,"E2"),sQuery(id+"F0.wireOp",EDGE,"E12.top"),sQuery(id+"F0.wireOp",EDGE,"E12.left"),sQuery(id+"F0.wireOp",EDGE,"E13.0.1.1"),sQuery(id+"F0.wireOp",EDGE,"E13.0.1.2"),sQuery(id+"F0.wireOp",EDGE,"E13.0.1.3"),sQuery(id+"F0.wireOp",EDGE,"E13.0.2.1"),sQuery(id+"F0.wireOp",EDGE,"E13.0.2.3"),sQuery(id+"F0.wireOp",EDGE,"E17.trimOffspring"),sQuery(id+"F0.wireOp",EDGE,"E20.5.0.0"),sQuery(id+"F0.wireOp",EDGE,"E20.5.0.1"),sQuery(id+"F0.wireOp",EDGE,"E20.5.0.2"),sQuery(id+"F0.wireOp",EDGE,"E20.6.0.0"),sQuery(id+"F0.wireOp",EDGE,"E20.6.0.1"),sQuery(id+"F0.wireOp",EDGE,"E20.6.0.2"),sQuery(id+"F0.wireOp",EDGE,"E20.7.0.0"),sQuery(id+"F0.wireOp",EDGE,"E20.7.0.1"),sQuery(id+"F0.wireOp",EDGE,"E20.7.0.2"),sQuery(id+"F0.wireOp",EDGE,"E20.8.0.0"),sQuery(id+"F0.wireOp",EDGE,"E20.8.0.1"),sQuery(id+"F0.wireOp",EDGE,"E20.8.0.2"),sQuery(id+"F0.wireOp",EDGE,"E20.9.0.0"),sQuery(id+"F0.wireOp",EDGE,"E20.9.0.2"),sQuery(id+"F0.wireOp",EDGE,"E24.trimOffspring"),sQuery(id+"F0.wireOp",EDGE,"E25.trimOffspring"),sQuery(id+"F0.wireOp",EDGE,"E26.trimOffspring"),sQuery(id+"F0.wireOp",EDGE,"E27.trimOffspring"),sQuery(id+"F0.wireOp",EDGE,"E28.trimOffspring")])]});
            var Q1;
            Q1=makeQuery(id+"F9.opExtrude","SWEPT_BODY",BODY,{"disambiguationData":[OSD([sQuery(id+"F3.wireOp",EDGE,"E29.bottom"),sQuery(id+"F3.wireOp",EDGE,"E29.left"),sQuery(id+"F3.wireOp",EDGE,"E29.right"),sQuery(id+"F3.wireOp",EDGE,"E30.top"),sQuery(id+"F3.wireOp",EDGE,"E30.right"),sQuery(id+"F3.wireOp",EDGE,"E32.1.0.0"),sQuery(id+"F3.wireOp",EDGE,"E32.1.0.1"),sQuery(id+"F3.wireOp",EDGE,"E32.1.0.2"),sQuery(id+"F3.wireOp",EDGE,"E32.2.0.0"),sQuery(id+"F3.wireOp",EDGE,"E32.2.0.1"),sQuery(id+"F3.wireOp",EDGE,"E32.2.0.2"),sQuery(id+"F3.wireOp",EDGE,"E32.3.0.0"),sQuery(id+"F3.wireOp",EDGE,"E32.3.0.1"),sQuery(id+"F3.wireOp",EDGE,"E32.3.0.2"),sQuery(id+"F3.wireOp",EDGE,"E32.4.0.0"),sQuery(id+"F3.wireOp",EDGE,"E32.4.0.1"),sQuery(id+"F3.wireOp",EDGE,"E32.4.0.2"),sQuery(id+"F3.wireOp",EDGE,"E34.trimOffspring"),sQuery(id+"F3.wireOp",EDGE,"E35.trimOffspring"),sQuery(id+"F3.wireOp",EDGE,"E36.trimOffspring"),sQuery(id+"F3.wireOp",EDGE,"E37.trimOffspring"),sQuery(id+"F3.wireOp",EDGE,"E42")])]});
            var Q2;
            Q2=makeQuery(id+"F5.opPattern","COPY",BODY,{"derivedFrom":makeQuery(id+"F2.opExtrude","SWEPT_BODY",BODY,{"disambiguationData":[OSD([sQuery(id+"F0.wireOp",EDGE,"E0.right"),sQuery(id+"F0.wireOp",EDGE,"E1"),sQuery(id+"F0.wireOp",EDGE,"E2"),sQuery(id+"F0.wireOp",EDGE,"E12.top"),sQuery(id+"F0.wireOp",EDGE,"E12.left"),sQuery(id+"F0.wireOp",EDGE,"E13.0.1.1"),sQuery(id+"F0.wireOp",EDGE,"E13.0.1.2"),sQuery(id+"F0.wireOp",EDGE,"E13.0.1.3"),sQuery(id+"F0.wireOp",EDGE,"E13.0.2.1"),sQuery(id+"F0.wireOp",EDGE,"E13.0.2.3"),sQuery(id+"F0.wireOp",EDGE,"E17.trimOffspring"),sQuery(id+"F0.wireOp",EDGE,"E20.5.0.0"),sQuery(id+"F0.wireOp",EDGE,"E20.5.0.1"),sQuery(id+"F0.wireOp",EDGE,"E20.5.0.2"),sQuery(id+"F0.wireOp",EDGE,"E20.6.0.0"),sQuery(id+"F0.wireOp",EDGE,"E20.6.0.1"),sQuery(id+"F0.wireOp",EDGE,"E20.6.0.2"),sQuery(id+"F0.wireOp",EDGE,"E20.7.0.0"),sQuery(id+"F0.wireOp",EDGE,"E20.7.0.1"),sQuery(id+"F0.wireOp",EDGE,"E20.7.0.2"),sQuery(id+"F0.wireOp",EDGE,"E20.8.0.0"),sQuery(id+"F0.wireOp",EDGE,"E20.8.0.1"),sQuery(id+"F0.wireOp",EDGE,"E20.8.0.2"),sQuery(id+"F0.wireOp",EDGE,"E20.9.0.0"),sQuery(id+"F0.wireOp",EDGE,"E20.9.0.2"),sQuery(id+"F0.wireOp",EDGE,"E24.trimOffspring"),sQuery(id+"F0.wireOp",EDGE,"E25.trimOffspring"),sQuery(id+"F0.wireOp",EDGE,"E26.trimOffspring"),sQuery(id+"F0.wireOp",EDGE,"E27.trimOffspring"),sQuery(id+"F0.wireOp",EDGE,"E28.trimOffspring")])]}),"instanceName":"1"});
            var Q3;
            Q3=makeQuery(id+"F14.opExtrude","SWEPT_BODY",BODY,{"disambiguationData":[OSD([sQuery(id+"F12.wireOp",EDGE,"E43.bottom"),sQuery(id+"F12.wireOp",EDGE,"E43.left"),sQuery(id+"F12.wireOp",EDGE,"E43.right"),sQuery(id+"F12.wireOp",EDGE,"E44")])]});
            booleanBodies(context, id + "F18", {"operationType" : BooleanOperationType.SUBTRACTION, "tools" : qUnion([Q0, Q1, Q2]), "targets" : qUnion([Q3]), "keepTools" : true});
        }
        {
            var Q0;
            Q0=makeQuery(id+"F2.opExtrude","SWEPT_BODY",BODY,{"disambiguationData":[OSD([sQuery(id+"F0.wireOp",EDGE,"E0.right"),sQuery(id+"F0.wireOp",EDGE,"E1"),sQuery(id+"F0.wireOp",EDGE,"E2"),sQuery(id+"F0.wireOp",EDGE,"E12.top"),sQuery(id+"F0.wireOp",EDGE,"E12.left"),sQuery(id+"F0.wireOp",EDGE,"E13.0.1.1"),sQuery(id+"F0.wireOp",EDGE,"E13.0.1.2"),sQuery(id+"F0.wireOp",EDGE,"E13.0.1.3"),sQuery(id+"F0.wireOp",EDGE,"E13.0.2.1"),sQuery(id+"F0.wireOp",EDGE,"E13.0.2.3"),sQuery(id+"F0.wireOp",EDGE,"E17.trimOffspring"),sQuery(id+"F0.wireOp",EDGE,"E20.5.0.0"),sQuery(id+"F0.wireOp",EDGE,"E20.5.0.1"),sQuery(id+"F0.wireOp",EDGE,"E20.5.0.2"),sQuery(id+"F0.wireOp",EDGE,"E20.6.0.0"),sQuery(id+"F0.wireOp",EDGE,"E20.6.0.1"),sQuery(id+"F0.wireOp",EDGE,"E20.6.0.2"),sQuery(id+"F0.wireOp",EDGE,"E20.7.0.0"),sQuery(id+"F0.wireOp",EDGE,"E20.7.0.1"),sQuery(id+"F0.wireOp",EDGE,"E20.7.0.2"),sQuery(id+"F0.wireOp",EDGE,"E20.8.0.0"),sQuery(id+"F0.wireOp",EDGE,"E20.8.0.1"),sQuery(id+"F0.wireOp",EDGE,"E20.8.0.2"),sQuery(id+"F0.wireOp",EDGE,"E20.9.0.0"),sQuery(id+"F0.wireOp",EDGE,"E20.9.0.2"),sQuery(id+"F0.wireOp",EDGE,"E24.trimOffspring"),sQuery(id+"F0.wireOp",EDGE,"E25.trimOffspring"),sQuery(id+"F0.wireOp",EDGE,"E26.trimOffspring"),sQuery(id+"F0.wireOp",EDGE,"E27.trimOffspring"),sQuery(id+"F0.wireOp",EDGE,"E28.trimOffspring")])]});
            deleteBodies(context, id + "F19", {"entities" : qUnion([Q0])});
        }
        {
            var Q0;
            Q0=makeQuery(id+"F5.opPattern","COPY",BODY,{"derivedFrom":makeQuery(id+"F2.opExtrude","SWEPT_BODY",BODY,{"disambiguationData":[OSD([sQuery(id+"F0.wireOp",EDGE,"E0.right"),sQuery(id+"F0.wireOp",EDGE,"E1"),sQuery(id+"F0.wireOp",EDGE,"E2"),sQuery(id+"F0.wireOp",EDGE,"E12.top"),sQuery(id+"F0.wireOp",EDGE,"E12.left"),sQuery(id+"F0.wireOp",EDGE,"E13.0.1.1"),sQuery(id+"F0.wireOp",EDGE,"E13.0.1.2"),sQuery(id+"F0.wireOp",EDGE,"E13.0.1.3"),sQuery(id+"F0.wireOp",EDGE,"E13.0.2.1"),sQuery(id+"F0.wireOp",EDGE,"E13.0.2.3"),sQuery(id+"F0.wireOp",EDGE,"E17.trimOffspring"),sQuery(id+"F0.wireOp",EDGE,"E20.5.0.0"),sQuery(id+"F0.wireOp",EDGE,"E20.5.0.1"),sQuery(id+"F0.wireOp",EDGE,"E20.5.0.2"),sQuery(id+"F0.wireOp",EDGE,"E20.6.0.0"),sQuery(id+"F0.wireOp",EDGE,"E20.6.0.1"),sQuery(id+"F0.wireOp",EDGE,"E20.6.0.2"),sQuery(id+"F0.wireOp",EDGE,"E20.7.0.0"),sQuery(id+"F0.wireOp",EDGE,"E20.7.0.1"),sQuery(id+"F0.wireOp",EDGE,"E20.7.0.2"),sQuery(id+"F0.wireOp",EDGE,"E20.8.0.0"),sQuery(id+"F0.wireOp",EDGE,"E20.8.0.1"),sQuery(id+"F0.wireOp",EDGE,"E20.8.0.2"),sQuery(id+"F0.wireOp",EDGE,"E20.9.0.0"),sQuery(id+"F0.wireOp",EDGE,"E20.9.0.2"),sQuery(id+"F0.wireOp",EDGE,"E24.trimOffspring"),sQuery(id+"F0.wireOp",EDGE,"E25.trimOffspring"),sQuery(id+"F0.wireOp",EDGE,"E26.trimOffspring"),sQuery(id+"F0.wireOp",EDGE,"E27.trimOffspring"),sQuery(id+"F0.wireOp",EDGE,"E28.trimOffspring")])]}),"instanceName":"1"});
            deleteBodies(context, id + "F20", {"entities" : qUnion([Q0])});
        }
        {
            var Q0;
            Q0=makeQuery(id+"F9.opExtrude","SWEPT_BODY",BODY,{"disambiguationData":[OSD([sQuery(id+"F3.wireOp",EDGE,"E29.bottom"),sQuery(id+"F3.wireOp",EDGE,"E29.left"),sQuery(id+"F3.wireOp",EDGE,"E29.right"),sQuery(id+"F3.wireOp",EDGE,"E30.top"),sQuery(id+"F3.wireOp",EDGE,"E30.right"),sQuery(id+"F3.wireOp",EDGE,"E32.1.0.0"),sQuery(id+"F3.wireOp",EDGE,"E32.1.0.1"),sQuery(id+"F3.wireOp",EDGE,"E32.1.0.2"),sQuery(id+"F3.wireOp",EDGE,"E32.2.0.0"),sQuery(id+"F3.wireOp",EDGE,"E32.2.0.1"),sQuery(id+"F3.wireOp",EDGE,"E32.2.0.2"),sQuery(id+"F3.wireOp",EDGE,"E32.3.0.0"),sQuery(id+"F3.wireOp",EDGE,"E32.3.0.1"),sQuery(id+"F3.wireOp",EDGE,"E32.3.0.2"),sQuery(id+"F3.wireOp",EDGE,"E32.4.0.0"),sQuery(id+"F3.wireOp",EDGE,"E32.4.0.1"),sQuery(id+"F3.wireOp",EDGE,"E32.4.0.2"),sQuery(id+"F3.wireOp",EDGE,"E34.trimOffspring"),sQuery(id+"F3.wireOp",EDGE,"E35.trimOffspring"),sQuery(id+"F3.wireOp",EDGE,"E36.trimOffspring"),sQuery(id+"F3.wireOp",EDGE,"E37.trimOffspring"),sQuery(id+"F3.wireOp",EDGE,"E42")])]});
            deleteBodies(context, id + "F21", {"entities" : qUnion([Q0])});
        }
        {
            var Q0;
            Q0=makeQuery(id+"F14.opExtrude","SWEPT_BODY",BODY,{"disambiguationData":[OSD([sQuery(id+"F12.wireOp",EDGE,"E43.bottom"),sQuery(id+"F12.wireOp",EDGE,"E43.left"),sQuery(id+"F12.wireOp",EDGE,"E43.right"),sQuery(id+"F12.wireOp",EDGE,"E44")])]});
            deleteBodies(context, id + "F22", {"entities" : qUnion([Q0])});
        }
        {
            var Q0;
            Q0=makeQuery(id+"F1.opExtrude","CAP_FACE",FACE,{"disambiguationData":[OSD([sQuery(id+"F0.wireOp",EDGE,"E0.bottom"),sQuery(id+"F0.wireOp",EDGE,"E0.top"),sQuery(id+"F0.wireOp",EDGE,"E0.left"),sQuery(id+"F0.wireOp",EDGE,"E1"),sQuery(id+"F0.wireOp",EDGE,"E2"),sQuery(id+"F0.wireOp",EDGE,"E3.bottom"),sQuery(id+"F0.wireOp",EDGE,"E3.top"),sQuery(id+"F0.wireOp",EDGE,"E3.right"),sQuery(id+"F0.wireOp",EDGE,"E4.trimOffspring"),sQuery(id+"F0.wireOp",EDGE,"E5.0.1.0"),sQuery(id+"F0.wireOp",EDGE,"E5.0.1.1"),sQuery(id+"F0.wireOp",EDGE,"E5.0.1.2"),sQuery(id+"F0.wireOp",EDGE,"E5.0.2.0"),sQuery(id+"F0.wireOp",EDGE,"E5.0.2.1"),sQuery(id+"F0.wireOp",EDGE,"E5.0.2.2"),sQuery(id+"F0.wireOp",EDGE,"E5.0.3.0"),sQuery(id+"F0.wireOp",EDGE,"E5.0.3.1"),sQuery(id+"F0.wireOp",EDGE,"E5.0.3.2"),sQuery(id+"F0.wireOp",EDGE,"E5.0.4.0"),sQuery(id+"F0.wireOp",EDGE,"E5.0.4.1"),sQuery(id+"F0.wireOp",EDGE,"E6.trimOffspring"),sQuery(id+"F0.wireOp",EDGE,"E7.trimOffspring"),sQuery(id+"F0.wireOp",EDGE,"E8.trimOffspring"),sQuery(id+"F0.wireOp",EDGE,"E9.top"),sQuery(id+"F0.wireOp",EDGE,"E9.left"),sQuery(id+"F0.wireOp",EDGE,"E9.right"),sQuery(id+"F0.wireOp",EDGE,"E11.1.0.0"),sQuery(id+"F0.wireOp",EDGE,"E11.1.0.1"),sQuery(id+"F0.wireOp",EDGE,"E10.trimOffspring"),sQuery(id+"F0.wireOp",EDGE,"E11.1.0.3"),sQuery(id+"F0.wireOp",EDGE,"E11.2.0.0"),sQuery(id+"F0.wireOp",EDGE,"E11.2.0.1"),sQuery(id+"F0.wireOp",EDGE,"E11.2.0.3"),sQuery(id+"F0.wireOp",EDGE,"E11.3.0.0"),sQuery(id+"F0.wireOp",EDGE,"E11.3.0.1"),sQuery(id+"F0.wireOp",EDGE,"E11.3.0.3"),sQuery(id+"F0.wireOp",EDGE,"E11.4.0.0"),sQuery(id+"F0.wireOp",EDGE,"E11.4.0.1"),sQuery(id+"F0.wireOp",EDGE,"E11.4.0.3"),sQuery(id+"F0.wireOp",EDGE,"E11.5.0.0"),sQuery(id+"F0.wireOp",EDGE,"E11.5.0.1"),sQuery(id+"F0.wireOp",EDGE,"E11.5.0.3"),sQuery(id+"F0.wireOp",EDGE,"E11.6.0.0"),sQuery(id+"F0.wireOp",EDGE,"E11.6.0.1"),sQuery(id+"F0.wireOp",EDGE,"E11.6.0.3"),sQuery(id+"F0.wireOp",EDGE,"E11.7.0.0"),sQuery(id+"F0.wireOp",EDGE,"E11.7.0.1"),sQuery(id+"F0.wireOp",EDGE,"E11.7.0.3"),sQuery(id+"F0.wireOp",EDGE,"E11.8.0.0"),sQuery(id+"F0.wireOp",EDGE,"E11.8.0.1"),sQuery(id+"F0.wireOp",EDGE,"E11.8.0.3"),sQuery(id+"F0.wireOp",EDGE,"E11.9.0.0"),sQuery(id+"F0.wireOp",EDGE,"E11.9.0.3"),sQuery(id+"F0.wireOp",EDGE,"E11.2.0.2"),sQuery(id+"F0.wireOp",EDGE,"E11.3.0.2"),sQuery(id+"F0.wireOp",EDGE,"E11.4.0.2"),sQuery(id+"F0.wireOp",EDGE,"E11.5.0.2"),sQuery(id+"F0.wireOp",EDGE,"E11.6.0.2"),sQuery(id+"F0.wireOp",EDGE,"E11.7.0.2"),sQuery(id+"F0.wireOp",EDGE,"E11.8.0.2"),sQuery(id+"F0.wireOp",EDGE,"E11.9.0.2"),sQuery(id+"F0.wireOp",EDGE,"E13.0.2.2"),sQuery(id+"F0.wireOp",EDGE,"E13.0.3.1"),sQuery(id+"F0.wireOp",EDGE,"E13.0.3.2"),sQuery(id+"F0.wireOp",EDGE,"E13.0.3.3"),sQuery(id+"F0.wireOp",EDGE,"E13.0.4.1"),sQuery(id+"F0.wireOp",EDGE,"E13.0.4.2"),sQuery(id+"F0.wireOp",EDGE,"E13.0.4.3"),sQuery(id+"F0.wireOp",EDGE,"E14.trimOffspring"),sQuery(id+"F0.wireOp",EDGE,"E15.trimOffspring"),sQuery(id+"F0.wireOp",EDGE,"E16.trimOffspring"),sQuery(id+"F0.wireOp",EDGE,"E18.top"),sQuery(id+"F0.wireOp",EDGE,"E18.left"),sQuery(id+"F0.wireOp",EDGE,"E18.right"),sQuery(id+"F0.wireOp",EDGE,"E19.trimOffspring"),sQuery(id+"F0.wireOp",EDGE,"E20.1.0.0"),sQuery(id+"F0.wireOp",EDGE,"E20.1.0.1"),sQuery(id+"F0.wireOp",EDGE,"E20.1.0.2"),sQuery(id+"F0.wireOp",EDGE,"E20.2.0.0"),sQuery(id+"F0.wireOp",EDGE,"E20.2.0.1"),sQuery(id+"F0.wireOp",EDGE,"E20.2.0.2"),sQuery(id+"F0.wireOp",EDGE,"E20.3.0.0"),sQuery(id+"F0.wireOp",EDGE,"E20.3.0.1"),sQuery(id+"F0.wireOp",EDGE,"E20.3.0.2"),sQuery(id+"F0.wireOp",EDGE,"E20.4.0.0"),sQuery(id+"F0.wireOp",EDGE,"E20.4.0.1"),sQuery(id+"F0.wireOp",EDGE,"E20.4.0.2"),sQuery(id+"F0.wireOp",EDGE,"E21.trimOffspring"),sQuery(id+"F0.wireOp",EDGE,"E22.trimOffspring"),sQuery(id+"F0.wireOp",EDGE,"E23.trimOffspring")])],"isStart":false});
            var sketch = newSketch(context, id + "F23", { "sketchPlane" : qUnion([Q0])});
            skCircle(sketch, "E45", {"center": v(188.75, -53.75) * mm, "radius": 1.25 * mm});
            skSolve(sketch);
        }
        {
            var Q0;
            Q0=makeQuery(id+"F23.imprint","IMPRINT",FACE,{"disambiguationData":[TD([[makeQuery(id+"F23.imprint","IMPRINT",EDGE,{"derivedFrom":sQuery(id+"F23.wireOp",EDGE,"E45")}),1.0]])]});
            extrude(context, id + "F24", {"entities" : qUnion([Q0]), "operationType" : NewBodyOperationType.ADD, "oppositeDirection" : true, "depth" : 100 * mm, "offsetDistance" : 25 * mm});
        }
        {
            var Q0;
            Q0=makeQuery(id+"F13.opExtrude","CAP_FACE",FACE,{"disambiguationData":[OSD([sQuery(id+"F12.wireOp",EDGE,"E43.top"),sQuery(id+"F12.wireOp",EDGE,"E43.left"),sQuery(id+"F12.wireOp",EDGE,"E43.right"),sQuery(id+"F12.wireOp",EDGE,"E44")])],"isStart":true});
            var sketch = newSketch(context, id + "F25", { "sketchPlane" : qUnion([Q0])});
            skCircle(sketch, "E46", {"center": v(-45.75, 71.25) * mm, "radius": 3.75 * mm});
            skSolve(sketch);
        }
        {
            var Q0;
            Q0=makeQuery(id+"F25.imprint","IMPRINT",FACE,{"disambiguationData":[TD([[makeQuery(id+"F25.imprint","IMPRINT",EDGE,{"derivedFrom":sQuery(id+"F25.wireOp",EDGE,"E46")}),1.0]])]});
            extrude(context, id + "F26", {"entities" : qUnion([Q0]), "operationType" : NewBodyOperationType.REMOVE, "oppositeDirection" : true, "depth" : 25 * mm, "offsetDistance" : 25 * mm});
        }
        {
            var Q0;
            Q0=makeQuery(id+"F13.opExtrude","CAP_FACE",FACE,{"disambiguationData":[OSD([sQuery(id+"F12.wireOp",EDGE,"E43.top"),sQuery(id+"F12.wireOp",EDGE,"E43.left"),sQuery(id+"F12.wireOp",EDGE,"E43.right"),sQuery(id+"F12.wireOp",EDGE,"E44")])],"isStart":true});
            var sketch = newSketch(context, id + "F27", { "sketchPlane" : qUnion([Q0])});
            skLineSegment(sketch, "E47.bottom", {"start": v(-57, 50) * mm, "end": v(-59.5, 50) * mm});
            skLineSegment(sketch, "E47.top", {"start": v(-57, 60) * mm, "end": v(-59.5, 60) * mm});
            skLineSegment(sketch, "E47.left", {"start": v(-57, 50) * mm, "end": v(-57, 60) * mm});
            skLineSegment(sketch, "E47.right", {"start": v(-59.5, 50) * mm, "end": v(-59.5, 60) * mm});
            skLineSegment(sketch, "E48.bottom", {"start": v(-57, 80) * mm, "end": v(-59.5, 80) * mm});
            skLineSegment(sketch, "E48.top", {"start": v(-57, 90) * mm, "end": v(-59.5, 90) * mm});
            skLineSegment(sketch, "E48.left", {"start": v(-57, 80) * mm, "end": v(-57, 90) * mm});
            skLineSegment(sketch, "E48.right", {"start": v(-59.5, 80) * mm, "end": v(-59.5, 90) * mm});
            skSolve(sketch);
        }
        {
            var Q0;
            Q0=makeQuery(id+"F27.imprint","IMPRINT",FACE,{"disambiguationData":[TD([[makeQuery(id+"F27.imprint","IMPRINT",EDGE,{"derivedFrom":sQuery(id+"F27.wireOp",EDGE,"E48.bottom")}),-1.0]])]});
            var Q1;
            Q1=makeQuery(id+"F27.imprint","IMPRINT",FACE,{"disambiguationData":[TD([[makeQuery(id+"F27.imprint","IMPRINT",EDGE,{"derivedFrom":sQuery(id+"F27.wireOp",EDGE,"E47.bottom")}),-1.0]])]});
            extrude(context, id + "F28", {"entities" : qUnion([Q0, Q1]), "operationType" : NewBodyOperationType.REMOVE, "oppositeDirection" : true, "depth" : 5 * mm, "offsetDistance" : 25 * mm});
        }
        {
            var Q0;
            Q0=makeQuery(id+"F13.opExtrude","CAP_FACE",FACE,{"disambiguationData":[OSD([sQuery(id+"F12.wireOp",EDGE,"E43.top"),sQuery(id+"F12.wireOp",EDGE,"E43.left"),sQuery(id+"F12.wireOp",EDGE,"E43.right"),sQuery(id+"F12.wireOp",EDGE,"E44")])],"isStart":true});
            var sketch = newSketch(context, id + "F29", { "sketchPlane" : qUnion([Q0])});
            skText(sketch, "E49", { "text": "on", "fontName": "OpenSans-Regular.ttf"});
            skText(sketch, "E50", { "text": "off", "fontName": "OpenSans-Regular.ttf"});
            const initialGuessF29  = {"E49": [-0.05293, 0.0811, 1, 0, 0.0081], "E50": [-0.05353, 0.05498, 1, 0, 0.00692]};
            skSetInitialGuess(sketch, initialGuessF29);
            skSolve(sketch);
        }
        {
            var Q0;
            Q0=makeQuery(id+"F29.imprint","IMPRINT",FACE,{"disambiguationData":[TD([[makeQuery(id+"F29.imprint","IMPRINT",EDGE,{"derivedFrom":sQuery(id+"F29.wireOp",EDGE,"E50.sketch_text.stroke-17")}),-1.0]])]});
            var Q1;
            Q1=makeQuery(id+"F29.imprint","IMPRINT",FACE,{"disambiguationData":[TD([[makeQuery(id+"F29.imprint","IMPRINT",EDGE,{"derivedFrom":sQuery(id+"F29.wireOp",EDGE,"E50.sketch_text.stroke-34")}),-1.0]])]});
            var Q2;
            Q2=makeQuery(id+"F29.imprint","IMPRINT",FACE,{"disambiguationData":[TD([[makeQuery(id+"F29.imprint","IMPRINT",EDGE,{"derivedFrom":sQuery(id+"F29.wireOp",EDGE,"E50.sketch_text.stroke-0")}),-1.0]])]});
            var Q3;
            Q3=makeQuery(id+"F29.imprint","IMPRINT",FACE,{"disambiguationData":[TD([[makeQuery(id+"F29.imprint","IMPRINT",EDGE,{"derivedFrom":sQuery(id+"F29.wireOp",EDGE,"E49.sketch_text.stroke-17")}),-1.0]])]});
            var Q4;
            Q4=makeQuery(id+"F29.imprint","IMPRINT",FACE,{"disambiguationData":[TD([[makeQuery(id+"F29.imprint","IMPRINT",EDGE,{"derivedFrom":sQuery(id+"F29.wireOp",EDGE,"E49.sketch_text.stroke-0")}),-1.0]])]});
            extrude(context, id + "F30", {"entities" : qUnion([Q0, Q1, Q2, Q3, Q4]), "operationType" : NewBodyOperationType.REMOVE, "oppositeDirection" : true, "depth" : 5 * mm, "offsetDistance" : 25 * mm});
        }
    });
